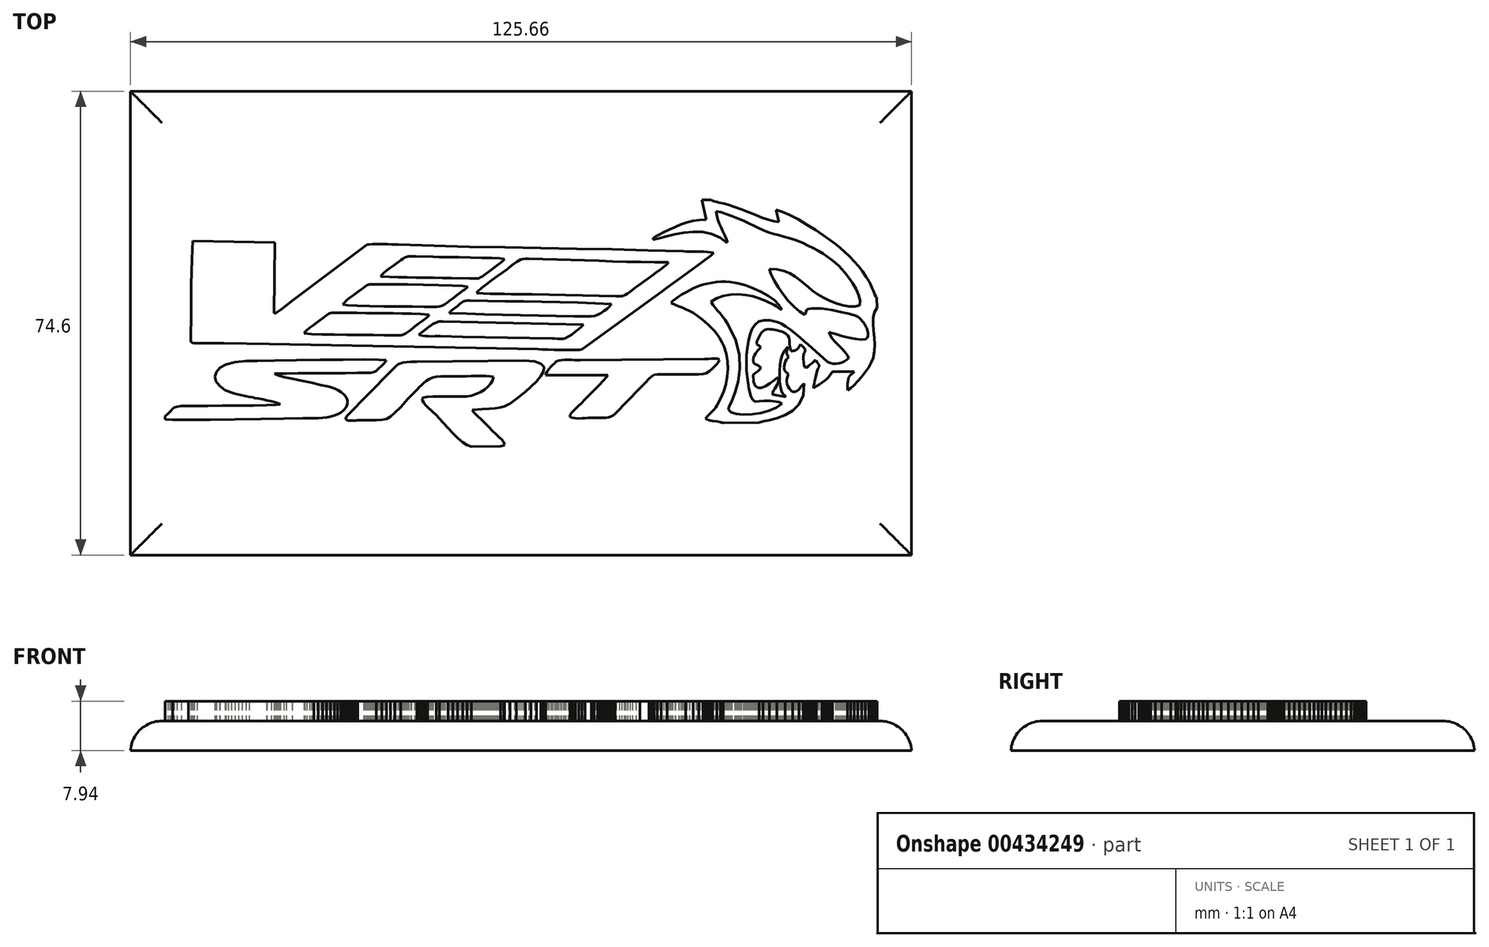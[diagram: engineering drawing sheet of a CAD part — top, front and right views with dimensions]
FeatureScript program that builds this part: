
annotation { "Feature Type Name" : "Feature", "Feature Type Description" : "" }
export const myFeature = defineFeature(function(context is Context, id is Id, definition is map)
    precondition{}
    {
        {
            var Q0;
            Q0=qCreatedBy(makeId("Top.planeOp"),FACE);
            var sketch = newSketch(context, id + "F0", { "sketchPlane" : qUnion([Q0])});
            skLineSegment(sketch, "E0.bottom", {"start": v(62.83, 37.3) * mm, "end": v(-62.83, 37.3) * mm});
            skLineSegment(sketch, "E0.top", {"start": v(62.83, -37.3) * mm, "end": v(-62.83, -37.3) * mm});
            skLineSegment(sketch, "E0.left", {"start": v(62.83, 37.3) * mm, "end": v(62.83, -37.3) * mm});
            skLineSegment(sketch, "E0.right", {"start": v(-62.83, 37.3) * mm, "end": v(-62.83, -37.3) * mm});
            skPoint(sketch, "E0.middle", {"position": v(0, 0) * mm});
            skSolve(sketch);
        }
        {
            var Q0;
            Q0=makeQuery(id+"F0.imprint","IMPRINT",FACE,{"disambiguationData":[TD([[makeQuery(id+"F0.imprint","IMPRINT",EDGE,{"derivedFrom":sQuery(id+"F0.wireOp",EDGE,"E0.bottom")}),1.0]])]});
            extrude(context, id + "F1", {"entities" : qUnion([Q0]), "depth" : 4.76 * mm});
        }
        {
            var Q0;
            Q0=makeQuery(id+"F1.opExtrude","CAP_FACE",FACE,{"disambiguationData":[OSD([sQuery(id+"F0.wireOp",EDGE,"E0.bottom"),sQuery(id+"F0.wireOp",EDGE,"E0.top"),sQuery(id+"F0.wireOp",EDGE,"E0.left"),sQuery(id+"F0.wireOp",EDGE,"E0.right")])],"isStart":false});
            var sketch = newSketch(context, id + "F2", { "sketchPlane" : qUnion([Q0])});
            skLineSegment(sketch, "E1", {"start": v(32.52, -16.06) * mm, "end": v(38.3, -16) * mm});
            skLineSegment(sketch, "E2", {"start": v(38.3, -16) * mm, "end": v(38.94, -15.8) * mm});
            skLineSegment(sketch, "E3", {"start": v(38.94, -15.8) * mm, "end": v(39.95, -15.58) * mm});
            skLineSegment(sketch, "E4", {"start": v(39.95, -15.58) * mm, "end": v(41.18, -15.27) * mm});
            skLineSegment(sketch, "E5", {"start": v(41.18, -15.27) * mm, "end": v(42.49, -14.8) * mm});
            skLineSegment(sketch, "E6", {"start": v(42.49, -14.8) * mm, "end": v(43.73, -14.08) * mm});
            skLineSegment(sketch, "E7", {"start": v(43.73, -14.08) * mm, "end": v(44.75, -13.04) * mm});
            skLineSegment(sketch, "E8", {"start": v(44.75, -13.04) * mm, "end": v(45.42, -11.6) * mm});
            skLineSegment(sketch, "E9", {"start": v(45.42, -11.6) * mm, "end": v(45.57, -9.7) * mm});
            skLineSegment(sketch, "E10", {"start": v(45.57, -9.7) * mm, "end": v(45.33, -9.86) * mm});
            skLineSegment(sketch, "E11", {"start": v(45.33, -9.86) * mm, "end": v(45.15, -10.05) * mm});
            skLineSegment(sketch, "E12", {"start": v(45.15, -10.05) * mm, "end": v(45, -10.27) * mm});
            skLineSegment(sketch, "E13", {"start": v(45, -10.27) * mm, "end": v(44.84, -10.5) * mm});
            skLineSegment(sketch, "E14", {"start": v(44.84, -10.5) * mm, "end": v(44.65, -10.7) * mm});
            skLineSegment(sketch, "E15", {"start": v(44.65, -10.7) * mm, "end": v(44.42, -10.88) * mm});
            skLineSegment(sketch, "E16", {"start": v(44.42, -10.88) * mm, "end": v(44.1, -11) * mm});
            skLineSegment(sketch, "E17", {"start": v(44.1, -11) * mm, "end": v(43.67, -11.04) * mm});
            skLineSegment(sketch, "E18", {"start": v(43.67, -11.04) * mm, "end": v(43.36, -10.77) * mm});
            skLineSegment(sketch, "E19", {"start": v(43.36, -10.77) * mm, "end": v(43.12, -10.48) * mm});
            skLineSegment(sketch, "E20", {"start": v(43.12, -10.48) * mm, "end": v(42.94, -10.16) * mm});
            skLineSegment(sketch, "E21", {"start": v(42.94, -10.16) * mm, "end": v(42.83, -9.81) * mm});
            skLineSegment(sketch, "E22", {"start": v(42.83, -9.81) * mm, "end": v(42.77, -9.44) * mm});
            skLineSegment(sketch, "E23", {"start": v(42.77, -9.44) * mm, "end": v(42.79, -9.04) * mm});
            skLineSegment(sketch, "E24", {"start": v(42.79, -9.04) * mm, "end": v(42.86, -8.61) * mm});
            skLineSegment(sketch, "E25", {"start": v(42.86, -8.61) * mm, "end": v(43, -8.16) * mm});
            skLineSegment(sketch, "E26", {"start": v(43, -8.16) * mm, "end": v(42.52, -7.74) * mm});
            skLineSegment(sketch, "E27", {"start": v(42.52, -7.74) * mm, "end": v(42.4, -7.47) * mm});
            skLineSegment(sketch, "E28", {"start": v(42.4, -7.47) * mm, "end": v(42.34, -7.16) * mm});
            skLineSegment(sketch, "E29", {"start": v(42.34, -7.16) * mm, "end": v(42.35, -6.83) * mm});
            skLineSegment(sketch, "E30", {"start": v(42.35, -6.83) * mm, "end": v(42.42, -6.5) * mm});
            skLineSegment(sketch, "E31", {"start": v(42.42, -6.5) * mm, "end": v(42.53, -6.18) * mm});
            skLineSegment(sketch, "E32", {"start": v(42.53, -6.18) * mm, "end": v(42.68, -5.89) * mm});
            skLineSegment(sketch, "E33", {"start": v(42.68, -5.89) * mm, "end": v(42.86, -5.64) * mm});
            skLineSegment(sketch, "E34", {"start": v(42.86, -5.64) * mm, "end": v(43.06, -5.47) * mm});
            skLineSegment(sketch, "E35", {"start": v(43.06, -5.47) * mm, "end": v(42.97, -5.3) * mm});
            skLineSegment(sketch, "E36", {"start": v(42.97, -5.3) * mm, "end": v(42.86, -5.14) * mm});
            skLineSegment(sketch, "E37", {"start": v(42.86, -5.14) * mm, "end": v(42.81, -5.05) * mm});
            skLineSegment(sketch, "E38", {"start": v(42.81, -5.05) * mm, "end": v(42.77, -4.95) * mm});
            skLineSegment(sketch, "E39", {"start": v(42.77, -4.95) * mm, "end": v(42.75, -4.82) * mm});
            skLineSegment(sketch, "E40", {"start": v(42.75, -4.82) * mm, "end": v(42.74, -4.67) * mm});
            skLineSegment(sketch, "E41", {"start": v(42.74, -4.67) * mm, "end": v(42.77, -4.5) * mm});
            skLineSegment(sketch, "E42", {"start": v(42.77, -4.5) * mm, "end": v(42.83, -4.3) * mm});
            skLineSegment(sketch, "E43", {"start": v(42.83, -4.3) * mm, "end": v(42.9, -4.08) * mm});
            skLineSegment(sketch, "E44", {"start": v(42.9, -4.08) * mm, "end": v(42.92, -3.8) * mm});
            skLineSegment(sketch, "E45", {"start": v(42.92, -3.8) * mm, "end": v(42.45, -4.38) * mm});
            skLineSegment(sketch, "E46", {"start": v(42.45, -4.38) * mm, "end": v(42.09, -5.08) * mm});
            skLineSegment(sketch, "E47", {"start": v(42.09, -5.08) * mm, "end": v(41.84, -5.87) * mm});
            skLineSegment(sketch, "E48", {"start": v(41.84, -5.87) * mm, "end": v(41.68, -6.72) * mm});
            skLineSegment(sketch, "E49", {"start": v(41.68, -6.72) * mm, "end": v(41.6, -7.6) * mm});
            skLineSegment(sketch, "E50", {"start": v(41.6, -7.6) * mm, "end": v(41.6, -8.5) * mm});
            skLineSegment(sketch, "E51", {"start": v(41.6, -8.5) * mm, "end": v(41.64, -9.35) * mm});
            skLineSegment(sketch, "E52", {"start": v(41.64, -9.35) * mm, "end": v(41.73, -10.15) * mm});
            skLineSegment(sketch, "E53", {"start": v(41.73, -10.15) * mm, "end": v(41.78, -10.49) * mm});
            skLineSegment(sketch, "E54", {"start": v(41.78, -10.49) * mm, "end": v(41.85, -10.75) * mm});
            skLineSegment(sketch, "E55", {"start": v(41.85, -10.75) * mm, "end": v(41.92, -10.97) * mm});
            skLineSegment(sketch, "E56", {"start": v(41.92, -10.97) * mm, "end": v(42.02, -11.15) * mm});
            skLineSegment(sketch, "E57", {"start": v(42.02, -11.15) * mm, "end": v(42.14, -11.3) * mm});
            skLineSegment(sketch, "E58", {"start": v(42.14, -11.3) * mm, "end": v(42.28, -11.46) * mm});
            skLineSegment(sketch, "E59", {"start": v(42.28, -11.46) * mm, "end": v(42.44, -11.63) * mm});
            skLineSegment(sketch, "E60", {"start": v(42.44, -11.63) * mm, "end": v(42.64, -11.82) * mm});
            skLineSegment(sketch, "E61", {"start": v(42.64, -11.82) * mm, "end": v(40.45, -11.46) * mm});
            skLineSegment(sketch, "E62", {"start": v(40.45, -11.46) * mm, "end": v(40.54, -11.1) * mm});
            skLineSegment(sketch, "E63", {"start": v(40.54, -11.1) * mm, "end": v(40.7, -10.78) * mm});
            skLineSegment(sketch, "E64", {"start": v(40.7, -10.78) * mm, "end": v(40.88, -10.5) * mm});
            skLineSegment(sketch, "E65", {"start": v(40.88, -10.5) * mm, "end": v(41.07, -10.2) * mm});
            skLineSegment(sketch, "E66", {"start": v(41.07, -10.2) * mm, "end": v(41.24, -9.9) * mm});
            skLineSegment(sketch, "E67", {"start": v(41.24, -9.9) * mm, "end": v(41.36, -9.55) * mm});
            skLineSegment(sketch, "E68", {"start": v(41.36, -9.55) * mm, "end": v(41.41, -9.14) * mm});
            skLineSegment(sketch, "E69", {"start": v(41.41, -9.14) * mm, "end": v(41.36, -8.65) * mm});
            skLineSegment(sketch, "E70", {"start": v(41.36, -8.65) * mm, "end": v(40.7, -9.2) * mm});
            skLineSegment(sketch, "E71", {"start": v(40.7, -9.2) * mm, "end": v(40, -9.71) * mm});
            skLineSegment(sketch, "E72", {"start": v(40, -9.71) * mm, "end": v(39.31, -10.13) * mm});
            skLineSegment(sketch, "E73", {"start": v(39.31, -10.13) * mm, "end": v(38.67, -10.37) * mm});
            skLineSegment(sketch, "E74", {"start": v(38.67, -10.37) * mm, "end": v(38.12, -10.38) * mm});
            skLineSegment(sketch, "E75", {"start": v(38.12, -10.38) * mm, "end": v(37.68, -10.08) * mm});
            skLineSegment(sketch, "E76", {"start": v(37.68, -10.08) * mm, "end": v(37.41, -9.41) * mm});
            skLineSegment(sketch, "E77", {"start": v(37.41, -9.41) * mm, "end": v(37.34, -8.3) * mm});
            skLineSegment(sketch, "E78", {"start": v(37.34, -8.3) * mm, "end": v(37.77, -8) * mm});
            skLineSegment(sketch, "E79", {"start": v(37.77, -8) * mm, "end": v(38.13, -7.73) * mm});
            skLineSegment(sketch, "E80", {"start": v(38.13, -7.73) * mm, "end": v(38.27, -7.6) * mm});
            skLineSegment(sketch, "E81", {"start": v(38.27, -7.6) * mm, "end": v(38.4, -7.47) * mm});
            skLineSegment(sketch, "E82", {"start": v(38.4, -7.47) * mm, "end": v(38.52, -7.31) * mm});
            skLineSegment(sketch, "E83", {"start": v(38.52, -7.31) * mm, "end": v(38.61, -7.13) * mm});
            skLineSegment(sketch, "E84", {"start": v(38.61, -7.13) * mm, "end": v(38.46, -7) * mm});
            skLineSegment(sketch, "E85", {"start": v(38.46, -7) * mm, "end": v(38.3, -6.9) * mm});
            skLineSegment(sketch, "E86", {"start": v(38.3, -6.9) * mm, "end": v(38.16, -6.82) * mm});
            skLineSegment(sketch, "E87", {"start": v(38.16, -6.82) * mm, "end": v(38, -6.74) * mm});
            skLineSegment(sketch, "E88", {"start": v(38, -6.74) * mm, "end": v(37.7, -6.57) * mm});
            skLineSegment(sketch, "E89", {"start": v(37.7, -6.57) * mm, "end": v(37.4, -6.36) * mm});
            skLineSegment(sketch, "E90", {"start": v(37.4, -6.36) * mm, "end": v(37.37, -5.9) * mm});
            skLineSegment(sketch, "E91", {"start": v(37.37, -5.9) * mm, "end": v(37.43, -5.51) * mm});
            skLineSegment(sketch, "E92", {"start": v(37.43, -5.51) * mm, "end": v(37.55, -5.17) * mm});
            skLineSegment(sketch, "E93", {"start": v(37.55, -5.17) * mm, "end": v(37.72, -4.86) * mm});
            skLineSegment(sketch, "E94", {"start": v(37.72, -4.86) * mm, "end": v(37.92, -4.6) * mm});
            skLineSegment(sketch, "E95", {"start": v(37.92, -4.6) * mm, "end": v(38.14, -4.36) * mm});
            skLineSegment(sketch, "E96", {"start": v(38.14, -4.36) * mm, "end": v(38.37, -4.13) * mm});
            skLineSegment(sketch, "E97", {"start": v(38.37, -4.13) * mm, "end": v(38.57, -3.92) * mm});
            skLineSegment(sketch, "E98", {"start": v(38.57, -3.92) * mm, "end": v(38.5, -3.8) * mm});
            skLineSegment(sketch, "E99", {"start": v(38.5, -3.8) * mm, "end": v(38.42, -3.71) * mm});
            skLineSegment(sketch, "E100", {"start": v(38.42, -3.71) * mm, "end": v(38.36, -3.65) * mm});
            skLineSegment(sketch, "E101", {"start": v(38.36, -3.65) * mm, "end": v(38.3, -3.6) * mm});
            skLineSegment(sketch, "E102", {"start": v(38.3, -3.6) * mm, "end": v(38.15, -3.5) * mm});
            skLineSegment(sketch, "E103", {"start": v(38.15, -3.5) * mm, "end": v(37.91, -3.32) * mm});
            skLineSegment(sketch, "E104", {"start": v(37.91, -3.32) * mm, "end": v(37.95, -3.08) * mm});
            skLineSegment(sketch, "E105", {"start": v(37.95, -3.08) * mm, "end": v(38.02, -2.82) * mm});
            skLineSegment(sketch, "E106", {"start": v(38.02, -2.82) * mm, "end": v(38.11, -2.56) * mm});
            skLineSegment(sketch, "E107", {"start": v(38.11, -2.56) * mm, "end": v(38.23, -2.3) * mm});
            skLineSegment(sketch, "E108", {"start": v(38.23, -2.3) * mm, "end": v(38.36, -2.05) * mm});
            skLineSegment(sketch, "E109", {"start": v(38.36, -2.05) * mm, "end": v(38.5, -1.82) * mm});
            skLineSegment(sketch, "E110", {"start": v(38.5, -1.82) * mm, "end": v(38.64, -1.6) * mm});
            skLineSegment(sketch, "E111", {"start": v(38.64, -1.6) * mm, "end": v(38.78, -1.43) * mm});
            skLineSegment(sketch, "E112", {"start": v(38.78, -1.43) * mm, "end": v(39, -1.22) * mm});
            skLineSegment(sketch, "E113", {"start": v(39, -1.22) * mm, "end": v(39.24, -1.08) * mm});
            skLineSegment(sketch, "E114", {"start": v(39.24, -1.08) * mm, "end": v(39.5, -1) * mm});
            skLineSegment(sketch, "E115", {"start": v(39.5, -1) * mm, "end": v(39.8, -0.96) * mm});
            skLineSegment(sketch, "E116", {"start": v(39.8, -0.96) * mm, "end": v(40.11, -0.96) * mm});
            skLineSegment(sketch, "E117", {"start": v(40.11, -0.96) * mm, "end": v(40.44, -1) * mm});
            skLineSegment(sketch, "E118", {"start": v(40.44, -1) * mm, "end": v(40.78, -1.06) * mm});
            skLineSegment(sketch, "E119", {"start": v(40.78, -1.06) * mm, "end": v(41.13, -1.13) * mm});
            skLineSegment(sketch, "E120", {"start": v(41.13, -1.13) * mm, "end": v(42.03, -1.38) * mm});
            skLineSegment(sketch, "E121", {"start": v(42.03, -1.38) * mm, "end": v(42.62, -1.66) * mm});
            skLineSegment(sketch, "E122", {"start": v(42.62, -1.66) * mm, "end": v(42.96, -1.98) * mm});
            skLineSegment(sketch, "E123", {"start": v(42.96, -1.98) * mm, "end": v(43.12, -2.35) * mm});
            skLineSegment(sketch, "E124", {"start": v(43.12, -2.35) * mm, "end": v(43.17, -2.77) * mm});
            skLineSegment(sketch, "E125", {"start": v(43.17, -2.77) * mm, "end": v(43.2, -3.26) * mm});
            skLineSegment(sketch, "E126", {"start": v(43.2, -3.26) * mm, "end": v(43.27, -3.83) * mm});
            skLineSegment(sketch, "E127", {"start": v(43.27, -3.83) * mm, "end": v(43.45, -4.48) * mm});
            skLineSegment(sketch, "E128", {"start": v(43.45, -4.48) * mm, "end": v(43.65, -4.47) * mm});
            skLineSegment(sketch, "E129", {"start": v(43.65, -4.47) * mm, "end": v(43.84, -4.44) * mm});
            skLineSegment(sketch, "E130", {"start": v(43.84, -4.44) * mm, "end": v(44.01, -4.4) * mm});
            skLineSegment(sketch, "E131", {"start": v(44.01, -4.4) * mm, "end": v(44.17, -4.34) * mm});
            skLineSegment(sketch, "E132", {"start": v(44.17, -4.34) * mm, "end": v(44.32, -4.26) * mm});
            skLineSegment(sketch, "E133", {"start": v(44.32, -4.26) * mm, "end": v(44.45, -4.16) * mm});
            skLineSegment(sketch, "E134", {"start": v(44.45, -4.16) * mm, "end": v(44.57, -4.04) * mm});
            skLineSegment(sketch, "E135", {"start": v(44.57, -4.04) * mm, "end": v(44.68, -3.9) * mm});
            skLineSegment(sketch, "E136", {"start": v(44.68, -3.9) * mm, "end": v(44.74, -3.8) * mm});
            skLineSegment(sketch, "E137", {"start": v(44.74, -3.8) * mm, "end": v(44.97, -3.39) * mm});
            skLineSegment(sketch, "E138", {"start": v(44.97, -3.39) * mm, "end": v(45.24, -3.66) * mm});
            skLineSegment(sketch, "E139", {"start": v(45.24, -3.66) * mm, "end": v(45.5, -3.9) * mm});
            skLineSegment(sketch, "E140", {"start": v(45.5, -3.9) * mm, "end": v(45.6, -4.04) * mm});
            skLineSegment(sketch, "E141", {"start": v(45.6, -4.04) * mm, "end": v(45.68, -4.19) * mm});
            skLineSegment(sketch, "E142", {"start": v(45.68, -4.19) * mm, "end": v(45.72, -4.35) * mm});
            skLineSegment(sketch, "E143", {"start": v(45.72, -4.35) * mm, "end": v(45.7, -4.55) * mm});
            skLineSegment(sketch, "E144", {"start": v(45.7, -4.55) * mm, "end": v(45.66, -4.7) * mm});
            skLineSegment(sketch, "E145", {"start": v(45.66, -4.7) * mm, "end": v(45.6, -4.77) * mm});
            skLineSegment(sketch, "E146", {"start": v(45.6, -4.77) * mm, "end": v(45.56, -4.83) * mm});
            skLineSegment(sketch, "E147", {"start": v(45.56, -4.83) * mm, "end": v(45.5, -4.9) * mm});
            skLineSegment(sketch, "E148", {"start": v(45.5, -4.9) * mm, "end": v(45.47, -5.05) * mm});
            skLineSegment(sketch, "E149", {"start": v(45.47, -5.05) * mm, "end": v(45.44, -5.3) * mm});
            skLineSegment(sketch, "E150", {"start": v(45.44, -5.3) * mm, "end": v(45.44, -5.71) * mm});
            skLineSegment(sketch, "E151", {"start": v(45.44, -5.71) * mm, "end": v(45.46, -6.32) * mm});
            skLineSegment(sketch, "E152", {"start": v(45.46, -6.32) * mm, "end": v(45.53, -6.85) * mm});
            skLineSegment(sketch, "E153", {"start": v(45.53, -6.85) * mm, "end": v(45.69, -7.1) * mm});
            skLineSegment(sketch, "E154", {"start": v(45.69, -7.1) * mm, "end": v(45.9, -7.12) * mm});
            skLineSegment(sketch, "E155", {"start": v(45.9, -7.12) * mm, "end": v(46.16, -6.98) * mm});
            skLineSegment(sketch, "E156", {"start": v(46.16, -6.98) * mm, "end": v(46.47, -6.73) * mm});
            skLineSegment(sketch, "E157", {"start": v(46.47, -6.73) * mm, "end": v(46.8, -6.44) * mm});
            skLineSegment(sketch, "E158", {"start": v(46.8, -6.44) * mm, "end": v(47.13, -6.16) * mm});
            skLineSegment(sketch, "E159", {"start": v(47.13, -6.16) * mm, "end": v(47.47, -5.97) * mm});
            skLineSegment(sketch, "E160", {"start": v(47.47, -5.97) * mm, "end": v(47.73, -6.38) * mm});
            skLineSegment(sketch, "E161", {"start": v(47.73, -6.38) * mm, "end": v(47.9, -6.64) * mm});
            skLineSegment(sketch, "E162", {"start": v(47.9, -6.64) * mm, "end": v(47.97, -6.8) * mm});
            skLineSegment(sketch, "E163", {"start": v(47.97, -6.8) * mm, "end": v(47.98, -6.9) * mm});
            skLineSegment(sketch, "E164", {"start": v(47.98, -6.9) * mm, "end": v(47.94, -7.02) * mm});
            skLineSegment(sketch, "E165", {"start": v(47.94, -7.02) * mm, "end": v(47.85, -7.2) * mm});
            skLineSegment(sketch, "E166", {"start": v(47.85, -7.2) * mm, "end": v(47.74, -7.49) * mm});
            skLineSegment(sketch, "E167", {"start": v(47.74, -7.49) * mm, "end": v(47.6, -7.94) * mm});
            skLineSegment(sketch, "E168", {"start": v(47.6, -7.94) * mm, "end": v(47.46, -8.5) * mm});
            skLineSegment(sketch, "E169", {"start": v(47.46, -8.5) * mm, "end": v(47.28, -9.23) * mm});
            skLineSegment(sketch, "E170", {"start": v(47.28, -9.23) * mm, "end": v(47.2, -9.6) * mm});
            skLineSegment(sketch, "E171", {"start": v(47.2, -9.6) * mm, "end": v(47.13, -9.95) * mm});
            skLineSegment(sketch, "E172", {"start": v(47.13, -9.95) * mm, "end": v(47.09, -10.25) * mm});
            skLineSegment(sketch, "E173", {"start": v(47.09, -10.25) * mm, "end": v(47.08, -10.48) * mm});
            skLineSegment(sketch, "E174", {"start": v(47.08, -10.48) * mm, "end": v(47.54, -10.15) * mm});
            skLineSegment(sketch, "E175", {"start": v(47.54, -10.15) * mm, "end": v(47.98, -9.86) * mm});
            skLineSegment(sketch, "E176", {"start": v(47.98, -9.86) * mm, "end": v(48.4, -9.58) * mm});
            skLineSegment(sketch, "E177", {"start": v(48.4, -9.58) * mm, "end": v(48.78, -9.3) * mm});
            skLineSegment(sketch, "E178", {"start": v(48.78, -9.3) * mm, "end": v(49.15, -8.99) * mm});
            skLineSegment(sketch, "E179", {"start": v(49.15, -8.99) * mm, "end": v(49.5, -8.65) * mm});
            skLineSegment(sketch, "E180", {"start": v(49.5, -8.65) * mm, "end": v(49.83, -8.25) * mm});
            skLineSegment(sketch, "E181", {"start": v(49.83, -8.25) * mm, "end": v(50.15, -7.77) * mm});
            skLineSegment(sketch, "E182", {"start": v(50.15, -7.77) * mm, "end": v(53.6, -7.78) * mm});
            skLineSegment(sketch, "E183", {"start": v(53.6, -7.78) * mm, "end": v(53.46, -7.99) * mm});
            skLineSegment(sketch, "E184", {"start": v(53.46, -7.99) * mm, "end": v(53.32, -8.13) * mm});
            skLineSegment(sketch, "E185", {"start": v(53.32, -8.13) * mm, "end": v(53.19, -8.24) * mm});
            skLineSegment(sketch, "E186", {"start": v(53.19, -8.24) * mm, "end": v(53.06, -8.32) * mm});
            skLineSegment(sketch, "E187", {"start": v(53.06, -8.32) * mm, "end": v(52.94, -8.42) * mm});
            skLineSegment(sketch, "E188", {"start": v(52.94, -8.42) * mm, "end": v(52.83, -8.54) * mm});
            skLineSegment(sketch, "E189", {"start": v(52.83, -8.54) * mm, "end": v(52.74, -8.72) * mm});
            skLineSegment(sketch, "E190", {"start": v(52.74, -8.72) * mm, "end": v(52.66, -8.97) * mm});
            skLineSegment(sketch, "E191", {"start": v(52.66, -8.97) * mm, "end": v(52.6, -9.36) * mm});
            skLineSegment(sketch, "E192", {"start": v(52.6, -9.36) * mm, "end": v(52.57, -9.85) * mm});
            skLineSegment(sketch, "E193", {"start": v(52.57, -9.85) * mm, "end": v(52.56, -10.35) * mm});
            skLineSegment(sketch, "E194", {"start": v(52.56, -10.35) * mm, "end": v(52.56, -10.77) * mm});
            skLineSegment(sketch, "E195", {"start": v(52.56, -10.77) * mm, "end": v(53.05, -10.44) * mm});
            skLineSegment(sketch, "E196", {"start": v(53.05, -10.44) * mm, "end": v(53.61, -9.95) * mm});
            skLineSegment(sketch, "E197", {"start": v(53.61, -9.95) * mm, "end": v(54.22, -9.33) * mm});
            skLineSegment(sketch, "E198", {"start": v(54.22, -9.33) * mm, "end": v(54.83, -8.63) * mm});
            skLineSegment(sketch, "E199", {"start": v(54.83, -8.63) * mm, "end": v(55.42, -7.88) * mm});
            skLineSegment(sketch, "E200", {"start": v(55.42, -7.88) * mm, "end": v(55.94, -7.1) * mm});
            skLineSegment(sketch, "E201", {"start": v(55.94, -7.1) * mm, "end": v(56.37, -6.35) * mm});
            skLineSegment(sketch, "E202", {"start": v(56.37, -6.35) * mm, "end": v(56.66, -5.65) * mm});
            skLineSegment(sketch, "E203", {"start": v(56.66, -5.65) * mm, "end": v(56.89, -4.58) * mm});
            skLineSegment(sketch, "E204", {"start": v(56.89, -4.58) * mm, "end": v(56.93, -3.46) * mm});
            skLineSegment(sketch, "E205", {"start": v(56.93, -3.46) * mm, "end": v(56.86, -2.33) * mm});
            skLineSegment(sketch, "E206", {"start": v(56.86, -2.33) * mm, "end": v(56.75, -1.2) * mm});
            skLineSegment(sketch, "E207", {"start": v(56.75, -1.2) * mm, "end": v(56.67, -0.13) * mm});
            skLineSegment(sketch, "E208", {"start": v(56.67, -0.13) * mm, "end": v(56.69, 0.86) * mm});
            skLineSegment(sketch, "E209", {"start": v(56.69, 0.86) * mm, "end": v(56.87, 1.74) * mm});
            skLineSegment(sketch, "E210", {"start": v(56.87, 1.74) * mm, "end": v(57.28, 2.48) * mm});
            skLineSegment(sketch, "E211", {"start": v(57.28, 2.48) * mm, "end": v(57.26, 4) * mm});
            skLineSegment(sketch, "E212", {"start": v(57.26, 4) * mm, "end": v(57.08, 4.3) * mm});
            skLineSegment(sketch, "E213", {"start": v(57.08, 4.3) * mm, "end": v(56.92, 4.62) * mm});
            skLineSegment(sketch, "E214", {"start": v(56.92, 4.62) * mm, "end": v(56.77, 4.95) * mm});
            skLineSegment(sketch, "E215", {"start": v(56.77, 4.95) * mm, "end": v(56.63, 5.3) * mm});
            skLineSegment(sketch, "E216", {"start": v(56.63, 5.3) * mm, "end": v(56.5, 5.65) * mm});
            skLineSegment(sketch, "E217", {"start": v(56.5, 5.65) * mm, "end": v(56.36, 6) * mm});
            skLineSegment(sketch, "E218", {"start": v(56.36, 6) * mm, "end": v(56.2, 6.34) * mm});
            skLineSegment(sketch, "E219", {"start": v(56.2, 6.34) * mm, "end": v(56.04, 6.67) * mm});
            skLineSegment(sketch, "E220", {"start": v(56.04, 6.67) * mm, "end": v(55.55, 7.48) * mm});
            skLineSegment(sketch, "E221", {"start": v(55.55, 7.48) * mm, "end": v(54.97, 8.31) * mm});
            skLineSegment(sketch, "E222", {"start": v(54.97, 8.31) * mm, "end": v(54.32, 9.14) * mm});
            skLineSegment(sketch, "E223", {"start": v(54.32, 9.14) * mm, "end": v(53.61, 9.96) * mm});
            skLineSegment(sketch, "E224", {"start": v(53.61, 9.96) * mm, "end": v(52.87, 10.74) * mm});
            skLineSegment(sketch, "E225", {"start": v(52.87, 10.74) * mm, "end": v(52.12, 11.47) * mm});
            skLineSegment(sketch, "E226", {"start": v(52.12, 11.47) * mm, "end": v(51.36, 12.14) * mm});
            skLineSegment(sketch, "E227", {"start": v(51.36, 12.14) * mm, "end": v(50.63, 12.72) * mm});
            skLineSegment(sketch, "E228", {"start": v(50.63, 12.72) * mm, "end": v(49.77, 13.35) * mm});
            skLineSegment(sketch, "E229", {"start": v(49.77, 13.35) * mm, "end": v(48.66, 14.12) * mm});
            skLineSegment(sketch, "E230", {"start": v(48.66, 14.12) * mm, "end": v(47.37, 14.98) * mm});
            skLineSegment(sketch, "E231", {"start": v(47.37, 14.98) * mm, "end": v(45.98, 15.86) * mm});
            skLineSegment(sketch, "E232", {"start": v(45.98, 15.86) * mm, "end": v(44.57, 16.7) * mm});
            skLineSegment(sketch, "E233", {"start": v(44.57, 16.7) * mm, "end": v(43.23, 17.42) * mm});
            skLineSegment(sketch, "E234", {"start": v(43.23, 17.42) * mm, "end": v(42.02, 17.96) * mm});
            skLineSegment(sketch, "E235", {"start": v(42.02, 17.96) * mm, "end": v(41.03, 18.26) * mm});
            skLineSegment(sketch, "E236", {"start": v(41.03, 18.26) * mm, "end": v(41.49, 16.25) * mm});
            skLineSegment(sketch, "E237", {"start": v(41.49, 16.25) * mm, "end": v(40.69, 16.4) * mm});
            skLineSegment(sketch, "E238", {"start": v(40.69, 16.4) * mm, "end": v(39.78, 16.65) * mm});
            skLineSegment(sketch, "E239", {"start": v(39.78, 16.65) * mm, "end": v(38.78, 17) * mm});
            skLineSegment(sketch, "E240", {"start": v(38.78, 17) * mm, "end": v(37.71, 17.41) * mm});
            skLineSegment(sketch, "E241", {"start": v(37.71, 17.41) * mm, "end": v(36.6, 17.85) * mm});
            skLineSegment(sketch, "E242", {"start": v(36.6, 17.85) * mm, "end": v(35.48, 18.3) * mm});
            skLineSegment(sketch, "E243", {"start": v(35.48, 18.3) * mm, "end": v(34.37, 18.72) * mm});
            skLineSegment(sketch, "E244", {"start": v(34.37, 18.72) * mm, "end": v(33.3, 19.09) * mm});
            skLineSegment(sketch, "E245", {"start": v(33.3, 19.09) * mm, "end": v(32.6, 19.26) * mm});
            skLineSegment(sketch, "E246", {"start": v(32.6, 19.26) * mm, "end": v(31.86, 19.4) * mm});
            skLineSegment(sketch, "E247", {"start": v(31.86, 19.4) * mm, "end": v(31.5, 19.49) * mm});
            skLineSegment(sketch, "E248", {"start": v(31.5, 19.49) * mm, "end": v(31.14, 19.58) * mm});
            skLineSegment(sketch, "E249", {"start": v(31.14, 19.58) * mm, "end": v(30.81, 19.7) * mm});
            skLineSegment(sketch, "E250", {"start": v(30.81, 19.7) * mm, "end": v(30.52, 19.83) * mm});
            skLineSegment(sketch, "E251", {"start": v(30.52, 19.83) * mm, "end": v(29.1, 19.81) * mm});
            skLineSegment(sketch, "E252", {"start": v(29.1, 19.81) * mm, "end": v(29.78, 16.66) * mm});
            skLineSegment(sketch, "E253", {"start": v(29.78, 16.66) * mm, "end": v(28.71, 16.62) * mm});
            skLineSegment(sketch, "E254", {"start": v(28.71, 16.62) * mm, "end": v(27.68, 16.46) * mm});
            skLineSegment(sketch, "E255", {"start": v(27.68, 16.46) * mm, "end": v(26.69, 16.2) * mm});
            skLineSegment(sketch, "E256", {"start": v(26.69, 16.2) * mm, "end": v(25.72, 15.87) * mm});
            skLineSegment(sketch, "E257", {"start": v(25.72, 15.87) * mm, "end": v(24.78, 15.47) * mm});
            skLineSegment(sketch, "E258", {"start": v(24.78, 15.47) * mm, "end": v(23.87, 15.05) * mm});
            skLineSegment(sketch, "E259", {"start": v(23.87, 15.05) * mm, "end": v(22.97, 14.6) * mm});
            skLineSegment(sketch, "E260", {"start": v(22.97, 14.6) * mm, "end": v(22.1, 14.16) * mm});
            skLineSegment(sketch, "E261", {"start": v(22.1, 14.16) * mm, "end": v(21.74, 13.99) * mm});
            skLineSegment(sketch, "E262", {"start": v(21.74, 13.99) * mm, "end": v(21.52, 13.87) * mm});
            skLineSegment(sketch, "E263", {"start": v(21.52, 13.87) * mm, "end": v(21.45, 13.8) * mm});
            skLineSegment(sketch, "E264", {"start": v(21.45, 13.8) * mm, "end": v(21.38, 13.7) * mm});
            skLineSegment(sketch, "E265", {"start": v(21.38, 13.7) * mm, "end": v(21.31, 13.58) * mm});
            skLineSegment(sketch, "E266", {"start": v(21.31, 13.58) * mm, "end": v(21.24, 13.4) * mm});
            skLineSegment(sketch, "E267", {"start": v(21.24, 13.4) * mm, "end": v(22.3, 13.65) * mm});
            skLineSegment(sketch, "E268", {"start": v(22.3, 13.65) * mm, "end": v(23.5, 13.96) * mm});
            skLineSegment(sketch, "E269", {"start": v(23.5, 13.96) * mm, "end": v(24.81, 14.3) * mm});
            skLineSegment(sketch, "E270", {"start": v(24.81, 14.3) * mm, "end": v(26.22, 14.56) * mm});
            skLineSegment(sketch, "E271", {"start": v(26.22, 14.56) * mm, "end": v(27.68, 14.7) * mm});
            skLineSegment(sketch, "E272", {"start": v(27.68, 14.7) * mm, "end": v(29.17, 14.66) * mm});
            skLineSegment(sketch, "E273", {"start": v(29.17, 14.66) * mm, "end": v(30.65, 14.35) * mm});
            skLineSegment(sketch, "E274", {"start": v(30.65, 14.35) * mm, "end": v(32.09, 13.72) * mm});
            skLineSegment(sketch, "E275", {"start": v(32.09, 13.72) * mm, "end": v(32.42, 13.5) * mm});
            skLineSegment(sketch, "E276", {"start": v(32.42, 13.5) * mm, "end": v(32.67, 13.3) * mm});
            skLineSegment(sketch, "E277", {"start": v(32.67, 13.3) * mm, "end": v(32.8, 13.21) * mm});
            skLineSegment(sketch, "E278", {"start": v(32.8, 13.21) * mm, "end": v(32.92, 13.13) * mm});
            skLineSegment(sketch, "E279", {"start": v(32.92, 13.13) * mm, "end": v(33.06, 13.04) * mm});
            skLineSegment(sketch, "E280", {"start": v(33.06, 13.04) * mm, "end": v(33.22, 12.97) * mm});
            skLineSegment(sketch, "E281", {"start": v(33.22, 12.97) * mm, "end": v(33.03, 13.54) * mm});
            skLineSegment(sketch, "E282", {"start": v(33.03, 13.54) * mm, "end": v(32.79, 14.14) * mm});
            skLineSegment(sketch, "E283", {"start": v(32.79, 14.14) * mm, "end": v(32.5, 14.76) * mm});
            skLineSegment(sketch, "E284", {"start": v(32.5, 14.76) * mm, "end": v(32.2, 15.4) * mm});
            skLineSegment(sketch, "E285", {"start": v(32.2, 15.4) * mm, "end": v(31.91, 16.05) * mm});
            skLineSegment(sketch, "E286", {"start": v(31.91, 16.05) * mm, "end": v(31.67, 16.7) * mm});
            skLineSegment(sketch, "E287", {"start": v(31.67, 16.7) * mm, "end": v(31.5, 17.36) * mm});
            skLineSegment(sketch, "E288", {"start": v(31.5, 17.36) * mm, "end": v(31.42, 18) * mm});
            skLineSegment(sketch, "E289", {"start": v(31.42, 18) * mm, "end": v(32.17, 17.84) * mm});
            skLineSegment(sketch, "E290", {"start": v(32.17, 17.84) * mm, "end": v(33.03, 17.58) * mm});
            skLineSegment(sketch, "E291", {"start": v(33.03, 17.58) * mm, "end": v(33.96, 17.24) * mm});
            skLineSegment(sketch, "E292", {"start": v(33.96, 17.24) * mm, "end": v(34.9, 16.85) * mm});
            skLineSegment(sketch, "E293", {"start": v(34.9, 16.85) * mm, "end": v(35.85, 16.44) * mm});
            skLineSegment(sketch, "E294", {"start": v(35.85, 16.44) * mm, "end": v(36.73, 16.03) * mm});
            skLineSegment(sketch, "E295", {"start": v(36.73, 16.03) * mm, "end": v(37.52, 15.65) * mm});
            skLineSegment(sketch, "E296", {"start": v(37.52, 15.65) * mm, "end": v(38.18, 15.3) * mm});
            skLineSegment(sketch, "E297", {"start": v(38.18, 15.3) * mm, "end": v(39, 14.92) * mm});
            skLineSegment(sketch, "E298", {"start": v(39, 14.92) * mm, "end": v(39.8, 14.62) * mm});
            skLineSegment(sketch, "E299", {"start": v(39.8, 14.62) * mm, "end": v(40.59, 14.39) * mm});
            skLineSegment(sketch, "E300", {"start": v(40.59, 14.39) * mm, "end": v(41.4, 14.18) * mm});
            skLineSegment(sketch, "E301", {"start": v(41.4, 14.18) * mm, "end": v(42.25, 13.96) * mm});
            skLineSegment(sketch, "E302", {"start": v(42.25, 13.96) * mm, "end": v(43.17, 13.7) * mm});
            skLineSegment(sketch, "E303", {"start": v(43.17, 13.7) * mm, "end": v(44.2, 13.34) * mm});
            skLineSegment(sketch, "E304", {"start": v(44.2, 13.34) * mm, "end": v(45.36, 12.88) * mm});
            skLineSegment(sketch, "E305", {"start": v(45.36, 12.88) * mm, "end": v(46.2, 12.5) * mm});
            skLineSegment(sketch, "E306", {"start": v(46.2, 12.5) * mm, "end": v(47.02, 12.09) * mm});
            skLineSegment(sketch, "E307", {"start": v(47.02, 12.09) * mm, "end": v(47.81, 11.65) * mm});
            skLineSegment(sketch, "E308", {"start": v(47.81, 11.65) * mm, "end": v(48.57, 11.19) * mm});
            skLineSegment(sketch, "E309", {"start": v(48.57, 11.19) * mm, "end": v(49.3, 10.7) * mm});
            skLineSegment(sketch, "E310", {"start": v(49.3, 10.7) * mm, "end": v(49.98, 10.2) * mm});
            skLineSegment(sketch, "E311", {"start": v(49.98, 10.2) * mm, "end": v(50.62, 9.68) * mm});
            skLineSegment(sketch, "E312", {"start": v(50.62, 9.68) * mm, "end": v(51.2, 9.14) * mm});
            skLineSegment(sketch, "E313", {"start": v(51.2, 9.14) * mm, "end": v(51.6, 8.73) * mm});
            skLineSegment(sketch, "E314", {"start": v(51.6, 8.73) * mm, "end": v(52.13, 8.11) * mm});
            skLineSegment(sketch, "E315", {"start": v(52.13, 8.11) * mm, "end": v(52.75, 7.33) * mm});
            skLineSegment(sketch, "E316", {"start": v(52.75, 7.33) * mm, "end": v(53.37, 6.45) * mm});
            skLineSegment(sketch, "E317", {"start": v(53.37, 6.45) * mm, "end": v(53.93, 5.5) * mm});
            skLineSegment(sketch, "E318", {"start": v(53.93, 5.5) * mm, "end": v(54.34, 4.56) * mm});
            skLineSegment(sketch, "E319", {"start": v(54.34, 4.56) * mm, "end": v(54.55, 3.66) * mm});
            skLineSegment(sketch, "E320", {"start": v(54.55, 3.66) * mm, "end": v(54.48, 2.85) * mm});
            skLineSegment(sketch, "E321", {"start": v(54.48, 2.85) * mm, "end": v(53.72, 2.67) * mm});
            skLineSegment(sketch, "E322", {"start": v(53.72, 2.67) * mm, "end": v(52.8, 2.69) * mm});
            skLineSegment(sketch, "E323", {"start": v(52.8, 2.69) * mm, "end": v(51.78, 2.87) * mm});
            skLineSegment(sketch, "E324", {"start": v(51.78, 2.87) * mm, "end": v(50.7, 3.2) * mm});
            skLineSegment(sketch, "E325", {"start": v(50.7, 3.2) * mm, "end": v(49.63, 3.62) * mm});
            skLineSegment(sketch, "E326", {"start": v(49.63, 3.62) * mm, "end": v(48.6, 4.12) * mm});
            skLineSegment(sketch, "E327", {"start": v(48.6, 4.12) * mm, "end": v(47.68, 4.66) * mm});
            skLineSegment(sketch, "E328", {"start": v(47.68, 4.66) * mm, "end": v(46.9, 5.22) * mm});
            skLineSegment(sketch, "E329", {"start": v(46.9, 5.22) * mm, "end": v(46.23, 5.78) * mm});
            skLineSegment(sketch, "E330", {"start": v(46.23, 5.78) * mm, "end": v(45.56, 6.37) * mm});
            skLineSegment(sketch, "E331", {"start": v(45.56, 6.37) * mm, "end": v(44.85, 6.96) * mm});
            skLineSegment(sketch, "E332", {"start": v(44.85, 6.96) * mm, "end": v(44.1, 7.5) * mm});
            skLineSegment(sketch, "E333", {"start": v(44.1, 7.5) * mm, "end": v(43.25, 8) * mm});
            skLineSegment(sketch, "E334", {"start": v(43.25, 8) * mm, "end": v(42.3, 8.38) * mm});
            skLineSegment(sketch, "E335", {"start": v(42.3, 8.38) * mm, "end": v(41.2, 8.64) * mm});
            skLineSegment(sketch, "E336", {"start": v(41.2, 8.64) * mm, "end": v(39.95, 8.75) * mm});
            skLineSegment(sketch, "E337", {"start": v(39.95, 8.75) * mm, "end": v(40.24, 7.87) * mm});
            skLineSegment(sketch, "E338", {"start": v(40.24, 7.87) * mm, "end": v(40.74, 6.86) * mm});
            skLineSegment(sketch, "E339", {"start": v(40.74, 6.86) * mm, "end": v(41.4, 5.76) * mm});
            skLineSegment(sketch, "E340", {"start": v(41.4, 5.76) * mm, "end": v(42.18, 4.66) * mm});
            skLineSegment(sketch, "E341", {"start": v(42.18, 4.66) * mm, "end": v(43.04, 3.6) * mm});
            skLineSegment(sketch, "E342", {"start": v(43.04, 3.6) * mm, "end": v(43.94, 2.65) * mm});
            skLineSegment(sketch, "E343", {"start": v(43.94, 2.65) * mm, "end": v(44.83, 1.89) * mm});
            skLineSegment(sketch, "E344", {"start": v(44.83, 1.89) * mm, "end": v(45.68, 1.37) * mm});
            skLineSegment(sketch, "E345", {"start": v(45.68, 1.37) * mm, "end": v(45.72, 1.47) * mm});
            skLineSegment(sketch, "E346", {"start": v(45.72, 1.47) * mm, "end": v(45.98, 2.25) * mm});
            skLineSegment(sketch, "E347", {"start": v(45.98, 2.25) * mm, "end": v(46.73, 2.36) * mm});
            skLineSegment(sketch, "E348", {"start": v(46.73, 2.36) * mm, "end": v(47.54, 2.4) * mm});
            skLineSegment(sketch, "E349", {"start": v(47.54, 2.4) * mm, "end": v(48.37, 2.35) * mm});
            skLineSegment(sketch, "E350", {"start": v(48.37, 2.35) * mm, "end": v(49.23, 2.24) * mm});
            skLineSegment(sketch, "E351", {"start": v(49.23, 2.24) * mm, "end": v(50.07, 2.1) * mm});
            skLineSegment(sketch, "E352", {"start": v(50.07, 2.1) * mm, "end": v(50.9, 1.93) * mm});
            skLineSegment(sketch, "E353", {"start": v(50.9, 1.93) * mm, "end": v(51.7, 1.75) * mm});
            skLineSegment(sketch, "E354", {"start": v(51.7, 1.75) * mm, "end": v(52.43, 1.59) * mm});
            skLineSegment(sketch, "E355", {"start": v(52.43, 1.59) * mm, "end": v(52.9, 1.48) * mm});
            skLineSegment(sketch, "E356", {"start": v(52.9, 1.48) * mm, "end": v(53.3, 1.38) * mm});
            skLineSegment(sketch, "E357", {"start": v(53.3, 1.38) * mm, "end": v(53.64, 1.27) * mm});
            skLineSegment(sketch, "E358", {"start": v(53.64, 1.27) * mm, "end": v(53.93, 1.15) * mm});
            skLineSegment(sketch, "E359", {"start": v(53.93, 1.15) * mm, "end": v(54.2, 1) * mm});
            skLineSegment(sketch, "E360", {"start": v(54.2, 1) * mm, "end": v(54.44, 0.83) * mm});
            skLineSegment(sketch, "E361", {"start": v(54.44, 0.83) * mm, "end": v(54.69, 0.6) * mm});
            skLineSegment(sketch, "E362", {"start": v(54.69, 0.6) * mm, "end": v(54.95, 0.3) * mm});
            skLineSegment(sketch, "E363", {"start": v(54.95, 0.3) * mm, "end": v(55.11, 0.1) * mm});
            skLineSegment(sketch, "E364", {"start": v(55.11, 0.1) * mm, "end": v(55.26, -0.12) * mm});
            skLineSegment(sketch, "E365", {"start": v(55.26, -0.12) * mm, "end": v(55.4, -0.35) * mm});
            skLineSegment(sketch, "E366", {"start": v(55.4, -0.35) * mm, "end": v(55.52, -0.58) * mm});
            skLineSegment(sketch, "E367", {"start": v(55.52, -0.58) * mm, "end": v(55.62, -0.83) * mm});
            skLineSegment(sketch, "E368", {"start": v(55.62, -0.83) * mm, "end": v(55.71, -1.08) * mm});
            skLineSegment(sketch, "E369", {"start": v(55.71, -1.08) * mm, "end": v(55.78, -1.33) * mm});
            skLineSegment(sketch, "E370", {"start": v(55.78, -1.33) * mm, "end": v(55.83, -1.6) * mm});
            skLineSegment(sketch, "E371", {"start": v(55.83, -1.6) * mm, "end": v(55.87, -1.96) * mm});
            skLineSegment(sketch, "E372", {"start": v(55.87, -1.96) * mm, "end": v(55.8, -2.27) * mm});
            skLineSegment(sketch, "E373", {"start": v(55.8, -2.27) * mm, "end": v(55.46, -2.56) * mm});
            skLineSegment(sketch, "E374", {"start": v(55.46, -2.56) * mm, "end": v(54.76, -2.63) * mm});
            skLineSegment(sketch, "E375", {"start": v(54.76, -2.63) * mm, "end": v(53.82, -2.54) * mm});
            skLineSegment(sketch, "E376", {"start": v(53.82, -2.54) * mm, "end": v(52.75, -2.33) * mm});
            skLineSegment(sketch, "E377", {"start": v(52.75, -2.33) * mm, "end": v(51.67, -2.06) * mm});
            skLineSegment(sketch, "E378", {"start": v(51.67, -2.06) * mm, "end": v(50.7, -1.78) * mm});
            skLineSegment(sketch, "E379", {"start": v(50.7, -1.78) * mm, "end": v(49.96, -1.55) * mm});
            skLineSegment(sketch, "E380", {"start": v(49.96, -1.55) * mm, "end": v(49.57, -1.43) * mm});
            skLineSegment(sketch, "E381", {"start": v(49.57, -1.43) * mm, "end": v(49.72, -1.9) * mm});
            skLineSegment(sketch, "E382", {"start": v(49.72, -1.9) * mm, "end": v(50.07, -2.44) * mm});
            skLineSegment(sketch, "E383", {"start": v(50.07, -2.44) * mm, "end": v(50.55, -3) * mm});
            skLineSegment(sketch, "E384", {"start": v(50.55, -3) * mm, "end": v(51.1, -3.56) * mm});
            skLineSegment(sketch, "E385", {"start": v(51.1, -3.56) * mm, "end": v(51.65, -4.13) * mm});
            skLineSegment(sketch, "E386", {"start": v(51.65, -4.13) * mm, "end": v(52.16, -4.67) * mm});
            skLineSegment(sketch, "E387", {"start": v(52.16, -4.67) * mm, "end": v(52.54, -5.17) * mm});
            skLineSegment(sketch, "E388", {"start": v(52.54, -5.17) * mm, "end": v(52.76, -5.61) * mm});
            skLineSegment(sketch, "E389", {"start": v(52.76, -5.61) * mm, "end": v(52.44, -5.9) * mm});
            skLineSegment(sketch, "E390", {"start": v(52.44, -5.9) * mm, "end": v(52.06, -6.14) * mm});
            skLineSegment(sketch, "E391", {"start": v(52.06, -6.14) * mm, "end": v(51.63, -6.33) * mm});
            skLineSegment(sketch, "E392", {"start": v(51.63, -6.33) * mm, "end": v(51.17, -6.46) * mm});
            skLineSegment(sketch, "E393", {"start": v(51.17, -6.46) * mm, "end": v(50.7, -6.52) * mm});
            skLineSegment(sketch, "E394", {"start": v(50.7, -6.52) * mm, "end": v(50.22, -6.5) * mm});
            skLineSegment(sketch, "E395", {"start": v(50.22, -6.5) * mm, "end": v(49.75, -6.4) * mm});
            skLineSegment(sketch, "E396", {"start": v(49.75, -6.4) * mm, "end": v(49.32, -6.21) * mm});
            skLineSegment(sketch, "E397", {"start": v(49.32, -6.21) * mm, "end": v(46.8, -4) * mm});
            skLineSegment(sketch, "E398", {"start": v(46.8, -4) * mm, "end": v(46.22, -3.48) * mm});
            skLineSegment(sketch, "E399", {"start": v(46.22, -3.48) * mm, "end": v(45.56, -2.9) * mm});
            skLineSegment(sketch, "E400", {"start": v(45.56, -2.9) * mm, "end": v(44.86, -2.28) * mm});
            skLineSegment(sketch, "E401", {"start": v(44.86, -2.28) * mm, "end": v(44.12, -1.66) * mm});
            skLineSegment(sketch, "E402", {"start": v(44.12, -1.66) * mm, "end": v(43.37, -1.07) * mm});
            skLineSegment(sketch, "E403", {"start": v(43.37, -1.07) * mm, "end": v(42.65, -0.55) * mm});
            skLineSegment(sketch, "E404", {"start": v(42.65, -0.55) * mm, "end": v(41.96, -0.13) * mm});
            skLineSegment(sketch, "E405", {"start": v(41.96, -0.13) * mm, "end": v(41.33, 0.14) * mm});
            skLineSegment(sketch, "E406", {"start": v(41.33, 0.14) * mm, "end": v(40.09, 0.46) * mm});
            skLineSegment(sketch, "E407", {"start": v(40.09, 0.46) * mm, "end": v(39.08, 0.49) * mm});
            skLineSegment(sketch, "E408", {"start": v(39.08, 0.49) * mm, "end": v(38.28, 0.26) * mm});
            skLineSegment(sketch, "E409", {"start": v(38.28, 0.26) * mm, "end": v(37.66, -0.22) * mm});
            skLineSegment(sketch, "E410", {"start": v(37.66, -0.22) * mm, "end": v(37.2, -0.91) * mm});
            skLineSegment(sketch, "E411", {"start": v(37.2, -0.91) * mm, "end": v(36.84, -1.8) * mm});
            skLineSegment(sketch, "E412", {"start": v(36.84, -1.8) * mm, "end": v(36.59, -2.87) * mm});
            skLineSegment(sketch, "E413", {"start": v(36.59, -2.87) * mm, "end": v(36.4, -4.1) * mm});
            skLineSegment(sketch, "E414", {"start": v(36.4, -4.1) * mm, "end": v(36.34, -4.62) * mm});
            skLineSegment(sketch, "E415", {"start": v(36.34, -4.62) * mm, "end": v(36.3, -5.18) * mm});
            skLineSegment(sketch, "E416", {"start": v(36.3, -5.18) * mm, "end": v(36.27, -5.76) * mm});
            skLineSegment(sketch, "E417", {"start": v(36.27, -5.76) * mm, "end": v(36.27, -6.36) * mm});
            skLineSegment(sketch, "E418", {"start": v(36.27, -6.36) * mm, "end": v(36.28, -6.95) * mm});
            skLineSegment(sketch, "E419", {"start": v(36.28, -6.95) * mm, "end": v(36.3, -7.53) * mm});
            skLineSegment(sketch, "E420", {"start": v(36.3, -7.53) * mm, "end": v(36.34, -8.1) * mm});
            skLineSegment(sketch, "E421", {"start": v(36.34, -8.1) * mm, "end": v(36.4, -8.64) * mm});
            skLineSegment(sketch, "E422", {"start": v(36.4, -8.64) * mm, "end": v(36.68, -10.55) * mm});
            skLineSegment(sketch, "E423", {"start": v(36.68, -10.55) * mm, "end": v(36.96, -11.74) * mm});
            skLineSegment(sketch, "E424", {"start": v(36.96, -11.74) * mm, "end": v(37.3, -12.37) * mm});
            skLineSegment(sketch, "E425", {"start": v(37.3, -12.37) * mm, "end": v(37.73, -12.6) * mm});
            skLineSegment(sketch, "E426", {"start": v(37.73, -12.6) * mm, "end": v(38.32, -12.58) * mm});
            skLineSegment(sketch, "E427", {"start": v(38.32, -12.58) * mm, "end": v(39.11, -12.48) * mm});
            skLineSegment(sketch, "E428", {"start": v(39.11, -12.48) * mm, "end": v(40.15, -12.46) * mm});
            skLineSegment(sketch, "E429", {"start": v(40.15, -12.46) * mm, "end": v(41.48, -12.67) * mm});
            skLineSegment(sketch, "E430", {"start": v(41.48, -12.67) * mm, "end": v(42, -12.9) * mm});
            skLineSegment(sketch, "E431", {"start": v(42, -12.9) * mm, "end": v(41.12, -13.57) * mm});
            skLineSegment(sketch, "E432", {"start": v(41.12, -13.57) * mm, "end": v(39.93, -14.08) * mm});
            skLineSegment(sketch, "E433", {"start": v(39.93, -14.08) * mm, "end": v(38.57, -14.44) * mm});
            skLineSegment(sketch, "E434", {"start": v(38.57, -14.44) * mm, "end": v(37.15, -14.63) * mm});
            skLineSegment(sketch, "E435", {"start": v(37.15, -14.63) * mm, "end": v(35.8, -14.68) * mm});
            skLineSegment(sketch, "E436", {"start": v(35.8, -14.68) * mm, "end": v(34.64, -14.57) * mm});
            skLineSegment(sketch, "E437", {"start": v(34.64, -14.57) * mm, "end": v(33.79, -14.31) * mm});
            skLineSegment(sketch, "E438", {"start": v(33.79, -14.31) * mm, "end": v(33.37, -13.9) * mm});
            skLineSegment(sketch, "E439", {"start": v(33.37, -13.9) * mm, "end": v(33.5, -13.45) * mm});
            skLineSegment(sketch, "E440", {"start": v(33.5, -13.45) * mm, "end": v(33.9, -12.5) * mm});
            skLineSegment(sketch, "E441", {"start": v(33.9, -12.5) * mm, "end": v(34.43, -11.14) * mm});
            skLineSegment(sketch, "E442", {"start": v(34.43, -11.14) * mm, "end": v(34.92, -9.4) * mm});
            skLineSegment(sketch, "E443", {"start": v(34.92, -9.4) * mm, "end": v(35.2, -7.37) * mm});
            skLineSegment(sketch, "E444", {"start": v(35.2, -7.37) * mm, "end": v(35.12, -5.07) * mm});
            skLineSegment(sketch, "E445", {"start": v(35.12, -5.07) * mm, "end": v(34.5, -2.6) * mm});
            skLineSegment(sketch, "E446", {"start": v(34.5, -2.6) * mm, "end": v(33.2, 0.03) * mm});
            skLineSegment(sketch, "E447", {"start": v(33.2, 0.03) * mm, "end": v(32.84, 0.54) * mm});
            skLineSegment(sketch, "E448", {"start": v(32.84, 0.54) * mm, "end": v(32.44, 1.07) * mm});
            skLineSegment(sketch, "E449", {"start": v(32.44, 1.07) * mm, "end": v(32.02, 1.6) * mm});
            skLineSegment(sketch, "E450", {"start": v(32.02, 1.6) * mm, "end": v(31.6, 2.09) * mm});
            skLineSegment(sketch, "E451", {"start": v(31.6, 2.09) * mm, "end": v(31.22, 2.54) * mm});
            skLineSegment(sketch, "E452", {"start": v(31.22, 2.54) * mm, "end": v(30.9, 2.93) * mm});
            skLineSegment(sketch, "E453", {"start": v(30.9, 2.93) * mm, "end": v(30.67, 3.25) * mm});
            skLineSegment(sketch, "E454", {"start": v(30.67, 3.25) * mm, "end": v(30.55, 3.48) * mm});
            skLineSegment(sketch, "E455", {"start": v(30.55, 3.48) * mm, "end": v(31.53, 4.02) * mm});
            skLineSegment(sketch, "E456", {"start": v(31.53, 4.02) * mm, "end": v(32.61, 4.38) * mm});
            skLineSegment(sketch, "E457", {"start": v(32.61, 4.38) * mm, "end": v(33.75, 4.58) * mm});
            skLineSegment(sketch, "E458", {"start": v(33.75, 4.58) * mm, "end": v(34.93, 4.63) * mm});
            skLineSegment(sketch, "E459", {"start": v(34.93, 4.63) * mm, "end": v(36.13, 4.54) * mm});
            skLineSegment(sketch, "E460", {"start": v(36.13, 4.54) * mm, "end": v(37.3, 4.32) * mm});
            skLineSegment(sketch, "E461", {"start": v(37.3, 4.32) * mm, "end": v(38.44, 3.98) * mm});
            skLineSegment(sketch, "E462", {"start": v(38.44, 3.98) * mm, "end": v(39.51, 3.54) * mm});
            skLineSegment(sketch, "E463", {"start": v(39.51, 3.54) * mm, "end": v(40.72, 2.92) * mm});
            skLineSegment(sketch, "E464", {"start": v(40.72, 2.92) * mm, "end": v(41.02, 2.73) * mm});
            skLineSegment(sketch, "E465", {"start": v(41.02, 2.73) * mm, "end": v(41.34, 2.52) * mm});
            skLineSegment(sketch, "E466", {"start": v(41.34, 2.52) * mm, "end": v(41.5, 2.42) * mm});
            skLineSegment(sketch, "E467", {"start": v(41.5, 2.42) * mm, "end": v(41.67, 2.32) * mm});
            skLineSegment(sketch, "E468", {"start": v(41.67, 2.32) * mm, "end": v(41.83, 2.24) * mm});
            skLineSegment(sketch, "E469", {"start": v(41.83, 2.24) * mm, "end": v(41.99, 2.17) * mm});
            skLineSegment(sketch, "E470", {"start": v(41.99, 2.17) * mm, "end": v(41.52, 2.93) * mm});
            skLineSegment(sketch, "E471", {"start": v(41.52, 2.93) * mm, "end": v(40.76, 3.68) * mm});
            skLineSegment(sketch, "E472", {"start": v(40.76, 3.68) * mm, "end": v(39.77, 4.4) * mm});
            skLineSegment(sketch, "E473", {"start": v(39.77, 4.4) * mm, "end": v(38.62, 5.06) * mm});
            skLineSegment(sketch, "E474", {"start": v(38.62, 5.06) * mm, "end": v(37.37, 5.64) * mm});
            skLineSegment(sketch, "E475", {"start": v(37.37, 5.64) * mm, "end": v(36.09, 6.12) * mm});
            skLineSegment(sketch, "E476", {"start": v(36.09, 6.12) * mm, "end": v(34.83, 6.46) * mm});
            skLineSegment(sketch, "E477", {"start": v(34.83, 6.46) * mm, "end": v(33.66, 6.65) * mm});
            skLineSegment(sketch, "E478", {"start": v(33.66, 6.65) * mm, "end": v(32.93, 6.7) * mm});
            skLineSegment(sketch, "E479", {"start": v(32.93, 6.7) * mm, "end": v(32.2, 6.68) * mm});
            skLineSegment(sketch, "E480", {"start": v(32.2, 6.68) * mm, "end": v(31.47, 6.63) * mm});
            skLineSegment(sketch, "E481", {"start": v(31.47, 6.63) * mm, "end": v(30.76, 6.53) * mm});
            skLineSegment(sketch, "E482", {"start": v(30.76, 6.53) * mm, "end": v(30.07, 6.4) * mm});
            skLineSegment(sketch, "E483", {"start": v(30.07, 6.4) * mm, "end": v(29.4, 6.22) * mm});
            skLineSegment(sketch, "E484", {"start": v(29.4, 6.22) * mm, "end": v(28.77, 6.03) * mm});
            skLineSegment(sketch, "E485", {"start": v(28.77, 6.03) * mm, "end": v(28.17, 5.8) * mm});
            skLineSegment(sketch, "E486", {"start": v(28.17, 5.8) * mm, "end": v(27.7, 5.6) * mm});
            skLineSegment(sketch, "E487", {"start": v(27.7, 5.6) * mm, "end": v(27.15, 5.32) * mm});
            skLineSegment(sketch, "E488", {"start": v(27.15, 5.32) * mm, "end": v(26.55, 4.99) * mm});
            skLineSegment(sketch, "E489", {"start": v(26.55, 4.99) * mm, "end": v(25.94, 4.63) * mm});
            skLineSegment(sketch, "E490", {"start": v(25.94, 4.63) * mm, "end": v(25.36, 4.25) * mm});
            skLineSegment(sketch, "E491", {"start": v(25.36, 4.25) * mm, "end": v(24.84, 3.89) * mm});
            skLineSegment(sketch, "E492", {"start": v(24.84, 3.89) * mm, "end": v(24.43, 3.55) * mm});
            skLineSegment(sketch, "E493", {"start": v(24.43, 3.55) * mm, "end": v(24.15, 3.26) * mm});
            skLineSegment(sketch, "E494", {"start": v(24.15, 3.26) * mm, "end": v(24.84, 2.94) * mm});
            skLineSegment(sketch, "E495", {"start": v(24.84, 2.94) * mm, "end": v(25.44, 2.7) * mm});
            skLineSegment(sketch, "E496", {"start": v(25.44, 2.7) * mm, "end": v(26, 2.48) * mm});
            skLineSegment(sketch, "E497", {"start": v(26, 2.48) * mm, "end": v(26.53, 2.25) * mm});
            skLineSegment(sketch, "E498", {"start": v(26.53, 2.25) * mm, "end": v(27.1, 1.99) * mm});
            skLineSegment(sketch, "E499", {"start": v(27.1, 1.99) * mm, "end": v(27.7, 1.64) * mm});
            skLineSegment(sketch, "E500", {"start": v(27.7, 1.64) * mm, "end": v(28.39, 1.18) * mm});
            skLineSegment(sketch, "E501", {"start": v(28.39, 1.18) * mm, "end": v(29.2, 0.57) * mm});
            skLineSegment(sketch, "E502", {"start": v(29.2, 0.57) * mm, "end": v(29.67, 0.17) * mm});
            skLineSegment(sketch, "E503", {"start": v(29.67, 0.17) * mm, "end": v(30.15, -0.26) * mm});
            skLineSegment(sketch, "E504", {"start": v(30.15, -0.26) * mm, "end": v(30.64, -0.74) * mm});
            skLineSegment(sketch, "E505", {"start": v(30.64, -0.74) * mm, "end": v(31.11, -1.26) * mm});
            skLineSegment(sketch, "E506", {"start": v(31.11, -1.26) * mm, "end": v(31.56, -1.82) * mm});
            skLineSegment(sketch, "E507", {"start": v(31.56, -1.82) * mm, "end": v(31.98, -2.42) * mm});
            skLineSegment(sketch, "E508", {"start": v(31.98, -2.42) * mm, "end": v(32.36, -3.06) * mm});
            skLineSegment(sketch, "E509", {"start": v(32.36, -3.06) * mm, "end": v(32.68, -3.75) * mm});
            skLineSegment(sketch, "E510", {"start": v(32.68, -3.75) * mm, "end": v(33.06, -4.9) * mm});
            skLineSegment(sketch, "E511", {"start": v(33.06, -4.9) * mm, "end": v(33.26, -6.1) * mm});
            skLineSegment(sketch, "E512", {"start": v(33.26, -6.1) * mm, "end": v(33.3, -7.35) * mm});
            skLineSegment(sketch, "E513", {"start": v(33.3, -7.35) * mm, "end": v(33.2, -8.6) * mm});
            skLineSegment(sketch, "E514", {"start": v(33.2, -8.6) * mm, "end": v(32.96, -9.84) * mm});
            skLineSegment(sketch, "E515", {"start": v(32.96, -9.84) * mm, "end": v(32.6, -11.04) * mm});
            skLineSegment(sketch, "E516", {"start": v(32.6, -11.04) * mm, "end": v(32.12, -12.18) * mm});
            skLineSegment(sketch, "E517", {"start": v(32.12, -12.18) * mm, "end": v(31.54, -13.23) * mm});
            skLineSegment(sketch, "E518", {"start": v(31.54, -13.23) * mm, "end": v(31.33, -13.54) * mm});
            skLineSegment(sketch, "E519", {"start": v(31.33, -13.54) * mm, "end": v(31.1, -13.83) * mm});
            skLineSegment(sketch, "E520", {"start": v(31.1, -13.83) * mm, "end": v(30.88, -14.1) * mm});
            skLineSegment(sketch, "E521", {"start": v(30.88, -14.1) * mm, "end": v(30.64, -14.35) * mm});
            skLineSegment(sketch, "E522", {"start": v(30.64, -14.35) * mm, "end": v(30.15, -14.84) * mm});
            skLineSegment(sketch, "E523", {"start": v(30.15, -14.84) * mm, "end": v(29.67, -15.32) * mm});
            skLineSegment(sketch, "E524", {"start": v(29.67, -15.32) * mm, "end": v(29.93, -15.48) * mm});
            skLineSegment(sketch, "E525", {"start": v(29.93, -15.48) * mm, "end": v(30.22, -15.58) * mm});
            skLineSegment(sketch, "E526", {"start": v(30.22, -15.58) * mm, "end": v(30.53, -15.66) * mm});
            skLineSegment(sketch, "E527", {"start": v(30.53, -15.66) * mm, "end": v(30.84, -15.72) * mm});
            skLineSegment(sketch, "E528", {"start": v(30.84, -15.72) * mm, "end": v(31.49, -15.8) * mm});
            skLineSegment(sketch, "E529", {"start": v(31.49, -15.8) * mm, "end": v(32.11, -15.92) * mm});
            skLineSegment(sketch, "E530", {"start": v(32.11, -15.92) * mm, "end": v(32.25, -15.96) * mm});
            skLineSegment(sketch, "E531", {"start": v(32.25, -15.96) * mm, "end": v(32.38, -16) * mm});
            skLineSegment(sketch, "E532", {"start": v(32.38, -16) * mm, "end": v(32.52, -16.06) * mm});
            skLineSegment(sketch, "E533", {"start": v(-4.42, -8.64) * mm, "end": v(-4.55, -9.19) * mm});
            skLineSegment(sketch, "E534", {"start": v(-4.55, -9.19) * mm, "end": v(-4.85, -9.72) * mm});
            skLineSegment(sketch, "E535", {"start": v(-4.85, -9.72) * mm, "end": v(-5.3, -10.22) * mm});
            skLineSegment(sketch, "E536", {"start": v(-5.3, -10.22) * mm, "end": v(-5.88, -10.68) * mm});
            skLineSegment(sketch, "E537", {"start": v(-5.88, -10.68) * mm, "end": v(-6.54, -11.08) * mm});
            skLineSegment(sketch, "E538", {"start": v(-6.54, -11.08) * mm, "end": v(-7.25, -11.4) * mm});
            skLineSegment(sketch, "E539", {"start": v(-7.25, -11.4) * mm, "end": v(-7.98, -11.64) * mm});
            skLineSegment(sketch, "E540", {"start": v(-7.98, -11.64) * mm, "end": v(-8.7, -11.77) * mm});
            skLineSegment(sketch, "E541", {"start": v(-8.7, -11.77) * mm, "end": v(-9.52, -11.8) * mm});
            skLineSegment(sketch, "E542", {"start": v(-9.52, -11.8) * mm, "end": v(-10.57, -11.8) * mm});
            skLineSegment(sketch, "E543", {"start": v(-10.57, -11.8) * mm, "end": v(-11.76, -11.77) * mm});
            skLineSegment(sketch, "E544", {"start": v(-11.76, -11.77) * mm, "end": v(-12.98, -11.76) * mm});
            skLineSegment(sketch, "E545", {"start": v(-12.98, -11.76) * mm, "end": v(-14.12, -11.77) * mm});
            skLineSegment(sketch, "E546", {"start": v(-14.12, -11.77) * mm, "end": v(-15.06, -11.83) * mm});
            skLineSegment(sketch, "E547", {"start": v(-15.06, -11.83) * mm, "end": v(-15.7, -11.96) * mm});
            skLineSegment(sketch, "E548", {"start": v(-15.7, -11.96) * mm, "end": v(-15.95, -12.19) * mm});
            skLineSegment(sketch, "E549", {"start": v(-15.95, -12.19) * mm, "end": v(-15.87, -12.45) * mm});
            skLineSegment(sketch, "E550", {"start": v(-15.87, -12.45) * mm, "end": v(-15.67, -12.77) * mm});
            skLineSegment(sketch, "E551", {"start": v(-15.67, -12.77) * mm, "end": v(-15.38, -13.11) * mm});
            skLineSegment(sketch, "E552", {"start": v(-15.38, -13.11) * mm, "end": v(-15.03, -13.48) * mm});
            skLineSegment(sketch, "E553", {"start": v(-15.03, -13.48) * mm, "end": v(-14.27, -14.2) * mm});
            skLineSegment(sketch, "E554", {"start": v(-14.27, -14.2) * mm, "end": v(-13.63, -14.8) * mm});
            skLineSegment(sketch, "E555", {"start": v(-13.63, -14.8) * mm, "end": v(-13.12, -15.36) * mm});
            skLineSegment(sketch, "E556", {"start": v(-13.12, -15.36) * mm, "end": v(-12.48, -16.07) * mm});
            skLineSegment(sketch, "E557", {"start": v(-12.48, -16.07) * mm, "end": v(-11.75, -16.88) * mm});
            skLineSegment(sketch, "E558", {"start": v(-11.75, -16.88) * mm, "end": v(-10.97, -17.7) * mm});
            skLineSegment(sketch, "E559", {"start": v(-10.97, -17.7) * mm, "end": v(-10.17, -18.48) * mm});
            skLineSegment(sketch, "E560", {"start": v(-10.17, -18.48) * mm, "end": v(-9.38, -19.13) * mm});
            skLineSegment(sketch, "E561", {"start": v(-9.38, -19.13) * mm, "end": v(-8.65, -19.6) * mm});
            skLineSegment(sketch, "E562", {"start": v(-8.65, -19.6) * mm, "end": v(-8, -19.83) * mm});
            skLineSegment(sketch, "E563", {"start": v(-8, -19.83) * mm, "end": v(-3.28, -19.8) * mm});
            skLineSegment(sketch, "E564", {"start": v(-3.28, -19.8) * mm, "end": v(-2.8, -19.68) * mm});
            skLineSegment(sketch, "E565", {"start": v(-2.8, -19.68) * mm, "end": v(-2.64, -19.46) * mm});
            skLineSegment(sketch, "E566", {"start": v(-2.64, -19.46) * mm, "end": v(-2.75, -19.16) * mm});
            skLineSegment(sketch, "E567", {"start": v(-2.75, -19.16) * mm, "end": v(-3.05, -18.77) * mm});
            skLineSegment(sketch, "E568", {"start": v(-3.05, -18.77) * mm, "end": v(-3.5, -18.33) * mm});
            skLineSegment(sketch, "E569", {"start": v(-3.5, -18.33) * mm, "end": v(-4.04, -17.84) * mm});
            skLineSegment(sketch, "E570", {"start": v(-4.04, -17.84) * mm, "end": v(-4.6, -17.31) * mm});
            skLineSegment(sketch, "E571", {"start": v(-4.6, -17.31) * mm, "end": v(-5.12, -16.76) * mm});
            skLineSegment(sketch, "E572", {"start": v(-5.12, -16.76) * mm, "end": v(-5.45, -16.4) * mm});
            skLineSegment(sketch, "E573", {"start": v(-5.45, -16.4) * mm, "end": v(-5.8, -16.04) * mm});
            skLineSegment(sketch, "E574", {"start": v(-5.8, -16.04) * mm, "end": v(-6.17, -15.7) * mm});
            skLineSegment(sketch, "E575", {"start": v(-6.17, -15.7) * mm, "end": v(-6.54, -15.35) * mm});
            skLineSegment(sketch, "E576", {"start": v(-6.54, -15.35) * mm, "end": v(-6.9, -15) * mm});
            skLineSegment(sketch, "E577", {"start": v(-6.9, -15) * mm, "end": v(-7.25, -14.66) * mm});
            skLineSegment(sketch, "E578", {"start": v(-7.25, -14.66) * mm, "end": v(-7.58, -14.31) * mm});
            skLineSegment(sketch, "E579", {"start": v(-7.58, -14.31) * mm, "end": v(-7.87, -13.96) * mm});
            skLineSegment(sketch, "E580", {"start": v(-7.87, -13.96) * mm, "end": v(-6.28, -13.8) * mm});
            skLineSegment(sketch, "E581", {"start": v(-6.28, -13.8) * mm, "end": v(-5.09, -13.73) * mm});
            skLineSegment(sketch, "E582", {"start": v(-5.09, -13.73) * mm, "end": v(-4.16, -13.69) * mm});
            skLineSegment(sketch, "E583", {"start": v(-4.16, -13.69) * mm, "end": v(-3.38, -13.6) * mm});
            skLineSegment(sketch, "E584", {"start": v(-3.38, -13.6) * mm, "end": v(-2.63, -13.36) * mm});
            skLineSegment(sketch, "E585", {"start": v(-2.63, -13.36) * mm, "end": v(-1.78, -12.9) * mm});
            skLineSegment(sketch, "E586", {"start": v(-1.78, -12.9) * mm, "end": v(-0.71, -12.15) * mm});
            skLineSegment(sketch, "E587", {"start": v(-0.71, -12.15) * mm, "end": v(0.7, -11.02) * mm});
            skLineSegment(sketch, "E588", {"start": v(0.7, -11.02) * mm, "end": v(1.63, -10.2) * mm});
            skLineSegment(sketch, "E589", {"start": v(1.63, -10.2) * mm, "end": v(2.5, -9.35) * mm});
            skLineSegment(sketch, "E590", {"start": v(2.5, -9.35) * mm, "end": v(3.21, -8.5) * mm});
            skLineSegment(sketch, "E591", {"start": v(3.21, -8.5) * mm, "end": v(3.64, -7.72) * mm});
            skLineSegment(sketch, "E592", {"start": v(3.64, -7.72) * mm, "end": v(3.68, -7.03) * mm});
            skLineSegment(sketch, "E593", {"start": v(3.68, -7.03) * mm, "end": v(3.22, -6.49) * mm});
            skLineSegment(sketch, "E594", {"start": v(3.22, -6.49) * mm, "end": v(2.17, -6.14) * mm});
            skLineSegment(sketch, "E595", {"start": v(2.17, -6.14) * mm, "end": v(0.4, -6.03) * mm});
            skLineSegment(sketch, "E596", {"start": v(0.4, -6.03) * mm, "end": v(-16.71, -6.2) * mm});
            skLineSegment(sketch, "E597", {"start": v(-16.71, -6.2) * mm, "end": v(-17.66, -6.22) * mm});
            skLineSegment(sketch, "E598", {"start": v(-17.66, -6.22) * mm, "end": v(-18.38, -6.25) * mm});
            skLineSegment(sketch, "E599", {"start": v(-18.38, -6.25) * mm, "end": v(-18.93, -6.31) * mm});
            skLineSegment(sketch, "E600", {"start": v(-18.93, -6.31) * mm, "end": v(-19.37, -6.43) * mm});
            skLineSegment(sketch, "E601", {"start": v(-19.37, -6.43) * mm, "end": v(-19.74, -6.61) * mm});
            skLineSegment(sketch, "E602", {"start": v(-19.74, -6.61) * mm, "end": v(-20.1, -6.89) * mm});
            skLineSegment(sketch, "E603", {"start": v(-20.1, -6.89) * mm, "end": v(-20.5, -7.27) * mm});
            skLineSegment(sketch, "E604", {"start": v(-20.5, -7.27) * mm, "end": v(-21, -7.77) * mm});
            skLineSegment(sketch, "E605", {"start": v(-21, -7.77) * mm, "end": v(-28.05, -14.96) * mm});
            skLineSegment(sketch, "E606", {"start": v(-28.05, -14.96) * mm, "end": v(-28.2, -15.27) * mm});
            skLineSegment(sketch, "E607", {"start": v(-28.2, -15.27) * mm, "end": v(-28.16, -15.47) * mm});
            skLineSegment(sketch, "E608", {"start": v(-28.16, -15.47) * mm, "end": v(-27.98, -15.6) * mm});
            skLineSegment(sketch, "E609", {"start": v(-27.98, -15.6) * mm, "end": v(-27.7, -15.66) * mm});
            skLineSegment(sketch, "E610", {"start": v(-27.7, -15.66) * mm, "end": v(-27.34, -15.67) * mm});
            skLineSegment(sketch, "E611", {"start": v(-27.34, -15.67) * mm, "end": v(-26.96, -15.66) * mm});
            skLineSegment(sketch, "E612", {"start": v(-26.96, -15.66) * mm, "end": v(-26.58, -15.63) * mm});
            skLineSegment(sketch, "E613", {"start": v(-26.58, -15.63) * mm, "end": v(-26.24, -15.62) * mm});
            skLineSegment(sketch, "E614", {"start": v(-26.24, -15.62) * mm, "end": v(-24.55, -15.61) * mm});
            skLineSegment(sketch, "E615", {"start": v(-24.55, -15.61) * mm, "end": v(-23.3, -15.61) * mm});
            skLineSegment(sketch, "E616", {"start": v(-23.3, -15.61) * mm, "end": v(-22.38, -15.56) * mm});
            skLineSegment(sketch, "E617", {"start": v(-22.38, -15.56) * mm, "end": v(-21.65, -15.38) * mm});
            skLineSegment(sketch, "E618", {"start": v(-21.65, -15.38) * mm, "end": v(-20.99, -15.02) * mm});
            skLineSegment(sketch, "E619", {"start": v(-20.99, -15.02) * mm, "end": v(-20.27, -14.4) * mm});
            skLineSegment(sketch, "E620", {"start": v(-20.27, -14.4) * mm, "end": v(-19.38, -13.49) * mm});
            skLineSegment(sketch, "E621", {"start": v(-19.38, -13.49) * mm, "end": v(-18.17, -12.2) * mm});
            skLineSegment(sketch, "E622", {"start": v(-18.17, -12.2) * mm, "end": v(-17.5, -11.48) * mm});
            skLineSegment(sketch, "E623", {"start": v(-17.5, -11.48) * mm, "end": v(-16.75, -10.69) * mm});
            skLineSegment(sketch, "E624", {"start": v(-16.75, -10.69) * mm, "end": v(-16.37, -10.3) * mm});
            skLineSegment(sketch, "E625", {"start": v(-16.37, -10.3) * mm, "end": v(-15.99, -9.92) * mm});
            skLineSegment(sketch, "E626", {"start": v(-15.99, -9.92) * mm, "end": v(-15.62, -9.58) * mm});
            skLineSegment(sketch, "E627", {"start": v(-15.62, -9.58) * mm, "end": v(-15.28, -9.29) * mm});
            skLineSegment(sketch, "E628", {"start": v(-15.28, -9.29) * mm, "end": v(-14.8, -8.98) * mm});
            skLineSegment(sketch, "E629", {"start": v(-14.8, -8.98) * mm, "end": v(-14.23, -8.77) * mm});
            skLineSegment(sketch, "E630", {"start": v(-14.23, -8.77) * mm, "end": v(-13.6, -8.64) * mm});
            skLineSegment(sketch, "E631", {"start": v(-13.6, -8.64) * mm, "end": v(-12.93, -8.57) * mm});
            skLineSegment(sketch, "E632", {"start": v(-12.93, -8.57) * mm, "end": v(-12.24, -8.55) * mm});
            skLineSegment(sketch, "E633", {"start": v(-12.24, -8.55) * mm, "end": v(-11.52, -8.56) * mm});
            skLineSegment(sketch, "E634", {"start": v(-11.52, -8.56) * mm, "end": v(-10.81, -8.57) * mm});
            skLineSegment(sketch, "E635", {"start": v(-10.81, -8.57) * mm, "end": v(-10.12, -8.57) * mm});
            skLineSegment(sketch, "E636", {"start": v(-10.12, -8.57) * mm, "end": v(-9.5, -8.56) * mm});
            skLineSegment(sketch, "E637", {"start": v(-9.5, -8.56) * mm, "end": v(-8.78, -8.54) * mm});
            skLineSegment(sketch, "E638", {"start": v(-8.78, -8.54) * mm, "end": v(-8, -8.52) * mm});
            skLineSegment(sketch, "E639", {"start": v(-8, -8.52) * mm, "end": v(-7.17, -8.5) * mm});
            skLineSegment(sketch, "E640", {"start": v(-7.17, -8.5) * mm, "end": v(-6.36, -8.5) * mm});
            skLineSegment(sketch, "E641", {"start": v(-6.36, -8.5) * mm, "end": v(-5.6, -8.52) * mm});
            skLineSegment(sketch, "E642", {"start": v(-5.6, -8.52) * mm, "end": v(-4.95, -8.56) * mm});
            skLineSegment(sketch, "E643", {"start": v(-4.95, -8.56) * mm, "end": v(-4.42, -8.64) * mm});
            skLineSegment(sketch, "E644", {"start": v(-57.28, -14.94) * mm, "end": v(-57.28, -15.45) * mm});
            skLineSegment(sketch, "E645", {"start": v(-57.28, -15.45) * mm, "end": v(-56.07, -15.52) * mm});
            skLineSegment(sketch, "E646", {"start": v(-56.07, -15.52) * mm, "end": v(-53.5, -15.54) * mm});
            skLineSegment(sketch, "E647", {"start": v(-53.5, -15.54) * mm, "end": v(-50, -15.52) * mm});
            skLineSegment(sketch, "E648", {"start": v(-50, -15.52) * mm, "end": v(-45.99, -15.47) * mm});
            skLineSegment(sketch, "E649", {"start": v(-45.99, -15.47) * mm, "end": v(-41.88, -15.41) * mm});
            skLineSegment(sketch, "E650", {"start": v(-41.88, -15.41) * mm, "end": v(-38.12, -15.36) * mm});
            skLineSegment(sketch, "E651", {"start": v(-38.12, -15.36) * mm, "end": v(-35.11, -15.3) * mm});
            skLineSegment(sketch, "E652", {"start": v(-35.11, -15.3) * mm, "end": v(-33.29, -15.29) * mm});
            skLineSegment(sketch, "E653", {"start": v(-33.29, -15.29) * mm, "end": v(-32.6, -15.27) * mm});
            skLineSegment(sketch, "E654", {"start": v(-32.6, -15.27) * mm, "end": v(-31.93, -15.22) * mm});
            skLineSegment(sketch, "E655", {"start": v(-31.93, -15.22) * mm, "end": v(-31.27, -15.14) * mm});
            skLineSegment(sketch, "E656", {"start": v(-31.27, -15.14) * mm, "end": v(-30.64, -15.02) * mm});
            skLineSegment(sketch, "E657", {"start": v(-30.64, -15.02) * mm, "end": v(-30.04, -14.86) * mm});
            skLineSegment(sketch, "E658", {"start": v(-30.04, -14.86) * mm, "end": v(-29.49, -14.64) * mm});
            skLineSegment(sketch, "E659", {"start": v(-29.49, -14.64) * mm, "end": v(-29, -14.37) * mm});
            skLineSegment(sketch, "E660", {"start": v(-29, -14.37) * mm, "end": v(-28.56, -14.04) * mm});
            skLineSegment(sketch, "E661", {"start": v(-28.56, -14.04) * mm, "end": v(-28.1, -13.5) * mm});
            skLineSegment(sketch, "E662", {"start": v(-28.1, -13.5) * mm, "end": v(-27.91, -12.95) * mm});
            skLineSegment(sketch, "E663", {"start": v(-27.91, -12.95) * mm, "end": v(-27.93, -12.43) * mm});
            skLineSegment(sketch, "E664", {"start": v(-27.93, -12.43) * mm, "end": v(-28.13, -11.93) * mm});
            skLineSegment(sketch, "E665", {"start": v(-28.13, -11.93) * mm, "end": v(-28.46, -11.47) * mm});
            skLineSegment(sketch, "E666", {"start": v(-28.46, -11.47) * mm, "end": v(-28.9, -11.07) * mm});
            skLineSegment(sketch, "E667", {"start": v(-28.9, -11.07) * mm, "end": v(-29.41, -10.74) * mm});
            skLineSegment(sketch, "E668", {"start": v(-29.41, -10.74) * mm, "end": v(-29.95, -10.5) * mm});
            skLineSegment(sketch, "E669", {"start": v(-29.95, -10.5) * mm, "end": v(-30.9, -10.22) * mm});
            skLineSegment(sketch, "E670", {"start": v(-30.9, -10.22) * mm, "end": v(-32.2, -9.92) * mm});
            skLineSegment(sketch, "E671", {"start": v(-32.2, -9.92) * mm, "end": v(-33.72, -9.6) * mm});
            skLineSegment(sketch, "E672", {"start": v(-33.72, -9.6) * mm, "end": v(-35.31, -9.28) * mm});
            skLineSegment(sketch, "E673", {"start": v(-35.31, -9.28) * mm, "end": v(-36.84, -8.96) * mm});
            skLineSegment(sketch, "E674", {"start": v(-36.84, -8.96) * mm, "end": v(-38.16, -8.65) * mm});
            skLineSegment(sketch, "E675", {"start": v(-38.16, -8.65) * mm, "end": v(-39.16, -8.37) * mm});
            skLineSegment(sketch, "E676", {"start": v(-39.16, -8.37) * mm, "end": v(-39.68, -8.13) * mm});
            skLineSegment(sketch, "E677", {"start": v(-39.68, -8.13) * mm, "end": v(-37.79, -8.08) * mm});
            skLineSegment(sketch, "E678", {"start": v(-37.79, -8.08) * mm, "end": v(-35.88, -8.05) * mm});
            skLineSegment(sketch, "E679", {"start": v(-35.88, -8.05) * mm, "end": v(-33.96, -8.04) * mm});
            skLineSegment(sketch, "E680", {"start": v(-33.96, -8.04) * mm, "end": v(-32.05, -8.04) * mm});
            skLineSegment(sketch, "E681", {"start": v(-32.05, -8.04) * mm, "end": v(-30.13, -8.04) * mm});
            skLineSegment(sketch, "E682", {"start": v(-30.13, -8.04) * mm, "end": v(-28.23, -8.03) * mm});
            skLineSegment(sketch, "E683", {"start": v(-28.23, -8.03) * mm, "end": v(-26.35, -8) * mm});
            skLineSegment(sketch, "E684", {"start": v(-26.35, -8) * mm, "end": v(-24.5, -7.96) * mm});
            skLineSegment(sketch, "E685", {"start": v(-24.5, -7.96) * mm, "end": v(-24.16, -7.95) * mm});
            skLineSegment(sketch, "E686", {"start": v(-24.16, -7.95) * mm, "end": v(-23.9, -7.92) * mm});
            skLineSegment(sketch, "E687", {"start": v(-23.9, -7.92) * mm, "end": v(-23.68, -7.87) * mm});
            skLineSegment(sketch, "E688", {"start": v(-23.68, -7.87) * mm, "end": v(-23.5, -7.8) * mm});
            skLineSegment(sketch, "E689", {"start": v(-23.5, -7.8) * mm, "end": v(-23.35, -7.7) * mm});
            skLineSegment(sketch, "E690", {"start": v(-23.35, -7.7) * mm, "end": v(-23.2, -7.59) * mm});
            skLineSegment(sketch, "E691", {"start": v(-23.2, -7.59) * mm, "end": v(-23.03, -7.43) * mm});
            skLineSegment(sketch, "E692", {"start": v(-23.03, -7.43) * mm, "end": v(-22.84, -7.24) * mm});
            skLineSegment(sketch, "E693", {"start": v(-22.84, -7.24) * mm, "end": v(-22.53, -6.96) * mm});
            skLineSegment(sketch, "E694", {"start": v(-22.53, -6.96) * mm, "end": v(-22.18, -6.63) * mm});
            skLineSegment(sketch, "E695", {"start": v(-22.18, -6.63) * mm, "end": v(-22.01, -6.46) * mm});
            skLineSegment(sketch, "E696", {"start": v(-22.01, -6.46) * mm, "end": v(-21.87, -6.28) * mm});
            skLineSegment(sketch, "E697", {"start": v(-21.87, -6.28) * mm, "end": v(-21.76, -6.1) * mm});
            skLineSegment(sketch, "E698", {"start": v(-21.76, -6.1) * mm, "end": v(-21.7, -5.94) * mm});
            skLineSegment(sketch, "E699", {"start": v(-21.7, -5.94) * mm, "end": v(-22.9, -5.86) * mm});
            skLineSegment(sketch, "E700", {"start": v(-22.9, -5.86) * mm, "end": v(-25.32, -5.84) * mm});
            skLineSegment(sketch, "E701", {"start": v(-25.32, -5.84) * mm, "end": v(-28.6, -5.86) * mm});
            skLineSegment(sketch, "E702", {"start": v(-28.6, -5.86) * mm, "end": v(-32.32, -5.9) * mm});
            skLineSegment(sketch, "E703", {"start": v(-32.32, -5.9) * mm, "end": v(-36.14, -5.96) * mm});
            skLineSegment(sketch, "E704", {"start": v(-36.14, -5.96) * mm, "end": v(-39.64, -6.01) * mm});
            skLineSegment(sketch, "E705", {"start": v(-39.64, -6.01) * mm, "end": v(-42.47, -6.06) * mm});
            skLineSegment(sketch, "E706", {"start": v(-42.47, -6.06) * mm, "end": v(-44.23, -6.09) * mm});
            skLineSegment(sketch, "E707", {"start": v(-44.23, -6.09) * mm, "end": v(-46.04, -6.23) * mm});
            skLineSegment(sketch, "E708", {"start": v(-46.04, -6.23) * mm, "end": v(-47.44, -6.61) * mm});
            skLineSegment(sketch, "E709", {"start": v(-47.44, -6.61) * mm, "end": v(-48.43, -7.17) * mm});
            skLineSegment(sketch, "E710", {"start": v(-48.43, -7.17) * mm, "end": v(-49.03, -7.85) * mm});
            skLineSegment(sketch, "E711", {"start": v(-49.03, -7.85) * mm, "end": v(-49.23, -8.6) * mm});
            skLineSegment(sketch, "E712", {"start": v(-49.23, -8.6) * mm, "end": v(-49.05, -9.37) * mm});
            skLineSegment(sketch, "E713", {"start": v(-49.05, -9.37) * mm, "end": v(-48.5, -10.1) * mm});
            skLineSegment(sketch, "E714", {"start": v(-48.5, -10.1) * mm, "end": v(-47.57, -10.75) * mm});
            skLineSegment(sketch, "E715", {"start": v(-47.57, -10.75) * mm, "end": v(-47.1, -10.97) * mm});
            skLineSegment(sketch, "E716", {"start": v(-47.1, -10.97) * mm, "end": v(-46.57, -11.16) * mm});
            skLineSegment(sketch, "E717", {"start": v(-46.57, -11.16) * mm, "end": v(-46.02, -11.32) * mm});
            skLineSegment(sketch, "E718", {"start": v(-46.02, -11.32) * mm, "end": v(-45.45, -11.46) * mm});
            skLineSegment(sketch, "E719", {"start": v(-45.45, -11.46) * mm, "end": v(-44.87, -11.6) * mm});
            skLineSegment(sketch, "E720", {"start": v(-44.87, -11.6) * mm, "end": v(-44.28, -11.7) * mm});
            skLineSegment(sketch, "E721", {"start": v(-44.28, -11.7) * mm, "end": v(-43.71, -11.83) * mm});
            skLineSegment(sketch, "E722", {"start": v(-43.71, -11.83) * mm, "end": v(-43.16, -11.94) * mm});
            skLineSegment(sketch, "E723", {"start": v(-43.16, -11.94) * mm, "end": v(-42.81, -12.02) * mm});
            skLineSegment(sketch, "E724", {"start": v(-42.81, -12.02) * mm, "end": v(-42.27, -12.12) * mm});
            skLineSegment(sketch, "E725", {"start": v(-42.27, -12.12) * mm, "end": v(-41.6, -12.26) * mm});
            skLineSegment(sketch, "E726", {"start": v(-41.6, -12.26) * mm, "end": v(-40.87, -12.41) * mm});
            skLineSegment(sketch, "E727", {"start": v(-40.87, -12.41) * mm, "end": v(-40.14, -12.58) * mm});
            skLineSegment(sketch, "E728", {"start": v(-40.14, -12.58) * mm, "end": v(-39.5, -12.75) * mm});
            skLineSegment(sketch, "E729", {"start": v(-39.5, -12.75) * mm, "end": v(-38.99, -12.91) * mm});
            skLineSegment(sketch, "E730", {"start": v(-38.99, -12.91) * mm, "end": v(-38.69, -13.06) * mm});
            skLineSegment(sketch, "E731", {"start": v(-38.69, -13.06) * mm, "end": v(-39.4, -13.14) * mm});
            skLineSegment(sketch, "E732", {"start": v(-39.4, -13.14) * mm, "end": v(-40.93, -13.2) * mm});
            skLineSegment(sketch, "E733", {"start": v(-40.93, -13.2) * mm, "end": v(-43.05, -13.23) * mm});
            skLineSegment(sketch, "E734", {"start": v(-43.05, -13.23) * mm, "end": v(-45.5, -13.26) * mm});
            skLineSegment(sketch, "E735", {"start": v(-45.5, -13.26) * mm, "end": v(-48.04, -13.28) * mm});
            skLineSegment(sketch, "E736", {"start": v(-48.04, -13.28) * mm, "end": v(-50.4, -13.29) * mm});
            skLineSegment(sketch, "E737", {"start": v(-50.4, -13.29) * mm, "end": v(-52.35, -13.3) * mm});
            skLineSegment(sketch, "E738", {"start": v(-52.35, -13.3) * mm, "end": v(-53.63, -13.3) * mm});
            skLineSegment(sketch, "E739", {"start": v(-53.63, -13.3) * mm, "end": v(-54.66, -13.34) * mm});
            skLineSegment(sketch, "E740", {"start": v(-54.66, -13.34) * mm, "end": v(-55.35, -13.43) * mm});
            skLineSegment(sketch, "E741", {"start": v(-55.35, -13.43) * mm, "end": v(-55.78, -13.58) * mm});
            skLineSegment(sketch, "E742", {"start": v(-55.78, -13.58) * mm, "end": v(-56.06, -13.78) * mm});
            skLineSegment(sketch, "E743", {"start": v(-56.06, -13.78) * mm, "end": v(-56.26, -14.02) * mm});
            skLineSegment(sketch, "E744", {"start": v(-56.26, -14.02) * mm, "end": v(-56.47, -14.3) * mm});
            skLineSegment(sketch, "E745", {"start": v(-56.47, -14.3) * mm, "end": v(-56.78, -14.6) * mm});
            skLineSegment(sketch, "E746", {"start": v(-56.78, -14.6) * mm, "end": v(-57.28, -14.94) * mm});
            skLineSegment(sketch, "E747", {"start": v(57.28, 2.48) * mm, "end": v(56.87, 1.74) * mm});
            skLineSegment(sketch, "E748", {"start": v(56.87, 1.74) * mm, "end": v(56.69, 0.86) * mm});
            skLineSegment(sketch, "E749", {"start": v(56.69, 0.86) * mm, "end": v(56.67, -0.13) * mm});
            skLineSegment(sketch, "E750", {"start": v(56.67, -0.13) * mm, "end": v(56.75, -1.2) * mm});
            skLineSegment(sketch, "E751", {"start": v(56.75, -1.2) * mm, "end": v(56.86, -2.33) * mm});
            skLineSegment(sketch, "E752", {"start": v(56.86, -2.33) * mm, "end": v(56.93, -3.46) * mm});
            skLineSegment(sketch, "E753", {"start": v(56.93, -3.46) * mm, "end": v(56.89, -4.58) * mm});
            skLineSegment(sketch, "E754", {"start": v(56.89, -4.58) * mm, "end": v(56.66, -5.65) * mm});
            skLineSegment(sketch, "E755", {"start": v(56.66, -5.65) * mm, "end": v(56.37, -6.35) * mm});
            skLineSegment(sketch, "E756", {"start": v(56.37, -6.35) * mm, "end": v(55.94, -7.1) * mm});
            skLineSegment(sketch, "E757", {"start": v(55.94, -7.1) * mm, "end": v(55.42, -7.88) * mm});
            skLineSegment(sketch, "E758", {"start": v(55.42, -7.88) * mm, "end": v(54.83, -8.63) * mm});
            skLineSegment(sketch, "E759", {"start": v(54.83, -8.63) * mm, "end": v(54.22, -9.33) * mm});
            skLineSegment(sketch, "E760", {"start": v(54.22, -9.33) * mm, "end": v(53.61, -9.95) * mm});
            skLineSegment(sketch, "E761", {"start": v(53.61, -9.95) * mm, "end": v(53.05, -10.44) * mm});
            skLineSegment(sketch, "E762", {"start": v(53.05, -10.44) * mm, "end": v(52.56, -10.77) * mm});
            skLineSegment(sketch, "E763", {"start": v(52.56, -10.77) * mm, "end": v(52.56, -10.35) * mm});
            skLineSegment(sketch, "E764", {"start": v(52.56, -10.35) * mm, "end": v(52.57, -9.85) * mm});
            skLineSegment(sketch, "E765", {"start": v(52.57, -9.85) * mm, "end": v(52.6, -9.36) * mm});
            skLineSegment(sketch, "E766", {"start": v(52.6, -9.36) * mm, "end": v(52.66, -8.97) * mm});
            skLineSegment(sketch, "E767", {"start": v(52.66, -8.97) * mm, "end": v(52.74, -8.72) * mm});
            skLineSegment(sketch, "E768", {"start": v(52.74, -8.72) * mm, "end": v(52.83, -8.54) * mm});
            skLineSegment(sketch, "E769", {"start": v(52.83, -8.54) * mm, "end": v(52.94, -8.42) * mm});
            skLineSegment(sketch, "E770", {"start": v(52.94, -8.42) * mm, "end": v(53.06, -8.32) * mm});
            skLineSegment(sketch, "E771", {"start": v(53.06, -8.32) * mm, "end": v(53.19, -8.24) * mm});
            skLineSegment(sketch, "E772", {"start": v(53.19, -8.24) * mm, "end": v(53.32, -8.13) * mm});
            skLineSegment(sketch, "E773", {"start": v(53.32, -8.13) * mm, "end": v(53.46, -7.99) * mm});
            skLineSegment(sketch, "E774", {"start": v(53.46, -7.99) * mm, "end": v(53.6, -7.78) * mm});
            skLineSegment(sketch, "E775", {"start": v(53.6, -7.78) * mm, "end": v(50.15, -7.77) * mm});
            skLineSegment(sketch, "E776", {"start": v(50.15, -7.77) * mm, "end": v(49.83, -8.25) * mm});
            skLineSegment(sketch, "E777", {"start": v(49.83, -8.25) * mm, "end": v(49.5, -8.65) * mm});
            skLineSegment(sketch, "E778", {"start": v(49.5, -8.65) * mm, "end": v(49.15, -8.99) * mm});
            skLineSegment(sketch, "E779", {"start": v(49.15, -8.99) * mm, "end": v(48.78, -9.3) * mm});
            skLineSegment(sketch, "E780", {"start": v(48.78, -9.3) * mm, "end": v(48.4, -9.58) * mm});
            skLineSegment(sketch, "E781", {"start": v(48.4, -9.58) * mm, "end": v(47.98, -9.86) * mm});
            skLineSegment(sketch, "E782", {"start": v(47.98, -9.86) * mm, "end": v(47.54, -10.15) * mm});
            skLineSegment(sketch, "E783", {"start": v(47.54, -10.15) * mm, "end": v(47.08, -10.48) * mm});
            skLineSegment(sketch, "E784", {"start": v(47.08, -10.48) * mm, "end": v(47.09, -10.25) * mm});
            skLineSegment(sketch, "E785", {"start": v(47.09, -10.25) * mm, "end": v(47.13, -9.95) * mm});
            skLineSegment(sketch, "E786", {"start": v(47.13, -9.95) * mm, "end": v(47.2, -9.6) * mm});
            skLineSegment(sketch, "E787", {"start": v(47.2, -9.6) * mm, "end": v(47.28, -9.23) * mm});
            skLineSegment(sketch, "E788", {"start": v(47.28, -9.23) * mm, "end": v(47.46, -8.5) * mm});
            skLineSegment(sketch, "E789", {"start": v(47.46, -8.5) * mm, "end": v(47.6, -7.94) * mm});
            skLineSegment(sketch, "E790", {"start": v(47.6, -7.94) * mm, "end": v(47.74, -7.49) * mm});
            skLineSegment(sketch, "E791", {"start": v(47.74, -7.49) * mm, "end": v(47.85, -7.2) * mm});
            skLineSegment(sketch, "E792", {"start": v(47.85, -7.2) * mm, "end": v(47.94, -7.02) * mm});
            skLineSegment(sketch, "E793", {"start": v(47.94, -7.02) * mm, "end": v(47.98, -6.9) * mm});
            skLineSegment(sketch, "E794", {"start": v(47.98, -6.9) * mm, "end": v(47.97, -6.8) * mm});
            skLineSegment(sketch, "E795", {"start": v(47.97, -6.8) * mm, "end": v(47.9, -6.64) * mm});
            skLineSegment(sketch, "E796", {"start": v(47.9, -6.64) * mm, "end": v(47.73, -6.38) * mm});
            skLineSegment(sketch, "E797", {"start": v(47.73, -6.38) * mm, "end": v(47.47, -5.97) * mm});
            skLineSegment(sketch, "E798", {"start": v(47.47, -5.97) * mm, "end": v(47.13, -6.16) * mm});
            skLineSegment(sketch, "E799", {"start": v(47.13, -6.16) * mm, "end": v(46.8, -6.44) * mm});
            skLineSegment(sketch, "E800", {"start": v(46.8, -6.44) * mm, "end": v(46.47, -6.73) * mm});
            skLineSegment(sketch, "E801", {"start": v(46.47, -6.73) * mm, "end": v(46.16, -6.98) * mm});
            skLineSegment(sketch, "E802", {"start": v(46.16, -6.98) * mm, "end": v(45.9, -7.12) * mm});
            skLineSegment(sketch, "E803", {"start": v(45.9, -7.12) * mm, "end": v(45.69, -7.1) * mm});
            skLineSegment(sketch, "E804", {"start": v(45.69, -7.1) * mm, "end": v(45.53, -6.85) * mm});
            skLineSegment(sketch, "E805", {"start": v(45.53, -6.85) * mm, "end": v(45.46, -6.32) * mm});
            skLineSegment(sketch, "E806", {"start": v(45.46, -6.32) * mm, "end": v(45.44, -5.71) * mm});
            skLineSegment(sketch, "E807", {"start": v(45.44, -5.71) * mm, "end": v(45.44, -5.3) * mm});
            skLineSegment(sketch, "E808", {"start": v(45.44, -5.3) * mm, "end": v(45.47, -5.05) * mm});
            skLineSegment(sketch, "E809", {"start": v(45.47, -5.05) * mm, "end": v(45.5, -4.9) * mm});
            skLineSegment(sketch, "E810", {"start": v(45.5, -4.9) * mm, "end": v(45.56, -4.83) * mm});
            skLineSegment(sketch, "E811", {"start": v(45.56, -4.83) * mm, "end": v(45.6, -4.77) * mm});
            skLineSegment(sketch, "E812", {"start": v(45.6, -4.77) * mm, "end": v(45.66, -4.7) * mm});
            skLineSegment(sketch, "E813", {"start": v(45.66, -4.7) * mm, "end": v(45.7, -4.55) * mm});
            skLineSegment(sketch, "E814", {"start": v(45.7, -4.55) * mm, "end": v(45.72, -4.35) * mm});
            skLineSegment(sketch, "E815", {"start": v(45.72, -4.35) * mm, "end": v(45.68, -4.19) * mm});
            skLineSegment(sketch, "E816", {"start": v(45.68, -4.19) * mm, "end": v(45.6, -4.04) * mm});
            skLineSegment(sketch, "E817", {"start": v(45.6, -4.04) * mm, "end": v(45.5, -3.9) * mm});
            skLineSegment(sketch, "E818", {"start": v(45.5, -3.9) * mm, "end": v(45.24, -3.66) * mm});
            skLineSegment(sketch, "E819", {"start": v(45.24, -3.66) * mm, "end": v(44.97, -3.39) * mm});
            skLineSegment(sketch, "E820", {"start": v(44.97, -3.39) * mm, "end": v(44.74, -3.8) * mm});
            skLineSegment(sketch, "E821", {"start": v(44.74, -3.8) * mm, "end": v(44.68, -3.9) * mm});
            skLineSegment(sketch, "E822", {"start": v(44.68, -3.9) * mm, "end": v(44.57, -4.04) * mm});
            skLineSegment(sketch, "E823", {"start": v(44.57, -4.04) * mm, "end": v(44.45, -4.16) * mm});
            skLineSegment(sketch, "E824", {"start": v(44.45, -4.16) * mm, "end": v(44.32, -4.26) * mm});
            skLineSegment(sketch, "E825", {"start": v(44.32, -4.26) * mm, "end": v(44.17, -4.34) * mm});
            skLineSegment(sketch, "E826", {"start": v(44.17, -4.34) * mm, "end": v(44.01, -4.4) * mm});
            skLineSegment(sketch, "E827", {"start": v(44.01, -4.4) * mm, "end": v(43.84, -4.44) * mm});
            skLineSegment(sketch, "E828", {"start": v(43.84, -4.44) * mm, "end": v(43.65, -4.47) * mm});
            skLineSegment(sketch, "E829", {"start": v(43.65, -4.47) * mm, "end": v(43.45, -4.48) * mm});
            skLineSegment(sketch, "E830", {"start": v(43.45, -4.48) * mm, "end": v(43.27, -3.83) * mm});
            skLineSegment(sketch, "E831", {"start": v(43.27, -3.83) * mm, "end": v(43.2, -3.26) * mm});
            skLineSegment(sketch, "E832", {"start": v(43.2, -3.26) * mm, "end": v(43.17, -2.77) * mm});
            skLineSegment(sketch, "E833", {"start": v(43.17, -2.77) * mm, "end": v(43.12, -2.35) * mm});
            skLineSegment(sketch, "E834", {"start": v(43.12, -2.35) * mm, "end": v(42.96, -1.98) * mm});
            skLineSegment(sketch, "E835", {"start": v(42.96, -1.98) * mm, "end": v(42.62, -1.66) * mm});
            skLineSegment(sketch, "E836", {"start": v(42.62, -1.66) * mm, "end": v(42.03, -1.38) * mm});
            skLineSegment(sketch, "E837", {"start": v(42.03, -1.38) * mm, "end": v(41.13, -1.13) * mm});
            skLineSegment(sketch, "E838", {"start": v(41.13, -1.13) * mm, "end": v(40.78, -1.06) * mm});
            skLineSegment(sketch, "E839", {"start": v(40.78, -1.06) * mm, "end": v(40.44, -1) * mm});
            skLineSegment(sketch, "E840", {"start": v(40.44, -1) * mm, "end": v(40.11, -0.96) * mm});
            skLineSegment(sketch, "E841", {"start": v(40.11, -0.96) * mm, "end": v(39.8, -0.96) * mm});
            skLineSegment(sketch, "E842", {"start": v(39.8, -0.96) * mm, "end": v(39.5, -1) * mm});
            skLineSegment(sketch, "E843", {"start": v(39.5, -1) * mm, "end": v(39.24, -1.08) * mm});
            skLineSegment(sketch, "E844", {"start": v(39.24, -1.08) * mm, "end": v(39, -1.22) * mm});
            skLineSegment(sketch, "E845", {"start": v(39, -1.22) * mm, "end": v(38.78, -1.43) * mm});
            skLineSegment(sketch, "E846", {"start": v(38.78, -1.43) * mm, "end": v(38.64, -1.6) * mm});
            skLineSegment(sketch, "E847", {"start": v(38.64, -1.6) * mm, "end": v(38.5, -1.82) * mm});
            skLineSegment(sketch, "E848", {"start": v(38.5, -1.82) * mm, "end": v(38.36, -2.05) * mm});
            skLineSegment(sketch, "E849", {"start": v(38.36, -2.05) * mm, "end": v(38.23, -2.3) * mm});
            skLineSegment(sketch, "E850", {"start": v(38.23, -2.3) * mm, "end": v(38.11, -2.56) * mm});
            skLineSegment(sketch, "E851", {"start": v(38.11, -2.56) * mm, "end": v(38.02, -2.82) * mm});
            skLineSegment(sketch, "E852", {"start": v(38.02, -2.82) * mm, "end": v(37.95, -3.08) * mm});
            skLineSegment(sketch, "E853", {"start": v(37.95, -3.08) * mm, "end": v(37.91, -3.32) * mm});
            skLineSegment(sketch, "E854", {"start": v(37.91, -3.32) * mm, "end": v(38.15, -3.5) * mm});
            skLineSegment(sketch, "E855", {"start": v(38.15, -3.5) * mm, "end": v(38.3, -3.6) * mm});
            skLineSegment(sketch, "E856", {"start": v(38.3, -3.6) * mm, "end": v(38.36, -3.65) * mm});
            skLineSegment(sketch, "E857", {"start": v(38.36, -3.65) * mm, "end": v(38.42, -3.71) * mm});
            skLineSegment(sketch, "E858", {"start": v(38.42, -3.71) * mm, "end": v(38.5, -3.8) * mm});
            skLineSegment(sketch, "E859", {"start": v(38.5, -3.8) * mm, "end": v(38.57, -3.92) * mm});
            skLineSegment(sketch, "E860", {"start": v(38.57, -3.92) * mm, "end": v(38.37, -4.13) * mm});
            skLineSegment(sketch, "E861", {"start": v(38.37, -4.13) * mm, "end": v(38.14, -4.36) * mm});
            skLineSegment(sketch, "E862", {"start": v(38.14, -4.36) * mm, "end": v(37.92, -4.6) * mm});
            skLineSegment(sketch, "E863", {"start": v(37.92, -4.6) * mm, "end": v(37.72, -4.86) * mm});
            skLineSegment(sketch, "E864", {"start": v(37.72, -4.86) * mm, "end": v(37.55, -5.17) * mm});
            skLineSegment(sketch, "E865", {"start": v(37.55, -5.17) * mm, "end": v(37.43, -5.51) * mm});
            skLineSegment(sketch, "E866", {"start": v(37.43, -5.51) * mm, "end": v(37.37, -5.9) * mm});
            skLineSegment(sketch, "E867", {"start": v(37.37, -5.9) * mm, "end": v(37.4, -6.36) * mm});
            skLineSegment(sketch, "E868", {"start": v(37.4, -6.36) * mm, "end": v(37.7, -6.57) * mm});
            skLineSegment(sketch, "E869", {"start": v(37.7, -6.57) * mm, "end": v(38, -6.74) * mm});
            skLineSegment(sketch, "E870", {"start": v(38, -6.74) * mm, "end": v(38.16, -6.82) * mm});
            skLineSegment(sketch, "E871", {"start": v(38.16, -6.82) * mm, "end": v(38.3, -6.9) * mm});
            skLineSegment(sketch, "E872", {"start": v(38.3, -6.9) * mm, "end": v(38.46, -7) * mm});
            skLineSegment(sketch, "E873", {"start": v(38.46, -7) * mm, "end": v(38.61, -7.13) * mm});
            skLineSegment(sketch, "E874", {"start": v(38.61, -7.13) * mm, "end": v(38.52, -7.31) * mm});
            skLineSegment(sketch, "E875", {"start": v(38.52, -7.31) * mm, "end": v(38.4, -7.47) * mm});
            skLineSegment(sketch, "E876", {"start": v(38.4, -7.47) * mm, "end": v(38.27, -7.6) * mm});
            skLineSegment(sketch, "E877", {"start": v(38.27, -7.6) * mm, "end": v(38.13, -7.73) * mm});
            skLineSegment(sketch, "E878", {"start": v(38.13, -7.73) * mm, "end": v(37.77, -8) * mm});
            skLineSegment(sketch, "E879", {"start": v(37.77, -8) * mm, "end": v(37.34, -8.3) * mm});
            skLineSegment(sketch, "E880", {"start": v(37.34, -8.3) * mm, "end": v(37.41, -9.41) * mm});
            skLineSegment(sketch, "E881", {"start": v(37.41, -9.41) * mm, "end": v(37.68, -10.08) * mm});
            skLineSegment(sketch, "E882", {"start": v(37.68, -10.08) * mm, "end": v(38.12, -10.38) * mm});
            skLineSegment(sketch, "E883", {"start": v(38.12, -10.38) * mm, "end": v(38.67, -10.37) * mm});
            skLineSegment(sketch, "E884", {"start": v(38.67, -10.37) * mm, "end": v(39.31, -10.13) * mm});
            skLineSegment(sketch, "E885", {"start": v(39.31, -10.13) * mm, "end": v(40, -9.71) * mm});
            skLineSegment(sketch, "E886", {"start": v(40, -9.71) * mm, "end": v(40.7, -9.2) * mm});
            skLineSegment(sketch, "E887", {"start": v(40.7, -9.2) * mm, "end": v(41.36, -8.65) * mm});
            skLineSegment(sketch, "E888", {"start": v(41.36, -8.65) * mm, "end": v(41.41, -9.14) * mm});
            skLineSegment(sketch, "E889", {"start": v(41.41, -9.14) * mm, "end": v(41.36, -9.55) * mm});
            skLineSegment(sketch, "E890", {"start": v(41.36, -9.55) * mm, "end": v(41.24, -9.9) * mm});
            skLineSegment(sketch, "E891", {"start": v(41.24, -9.9) * mm, "end": v(41.07, -10.2) * mm});
            skLineSegment(sketch, "E892", {"start": v(41.07, -10.2) * mm, "end": v(40.88, -10.5) * mm});
            skLineSegment(sketch, "E893", {"start": v(40.88, -10.5) * mm, "end": v(40.7, -10.78) * mm});
            skLineSegment(sketch, "E894", {"start": v(40.7, -10.78) * mm, "end": v(40.54, -11.1) * mm});
            skLineSegment(sketch, "E895", {"start": v(40.54, -11.1) * mm, "end": v(40.45, -11.46) * mm});
            skLineSegment(sketch, "E896", {"start": v(40.45, -11.46) * mm, "end": v(42.64, -11.82) * mm});
            skLineSegment(sketch, "E897", {"start": v(42.64, -11.82) * mm, "end": v(42.44, -11.63) * mm});
            skLineSegment(sketch, "E898", {"start": v(42.44, -11.63) * mm, "end": v(42.28, -11.46) * mm});
            skLineSegment(sketch, "E899", {"start": v(42.28, -11.46) * mm, "end": v(42.14, -11.3) * mm});
            skLineSegment(sketch, "E900", {"start": v(42.14, -11.3) * mm, "end": v(42.02, -11.15) * mm});
            skLineSegment(sketch, "E901", {"start": v(42.02, -11.15) * mm, "end": v(41.92, -10.97) * mm});
            skLineSegment(sketch, "E902", {"start": v(41.92, -10.97) * mm, "end": v(41.85, -10.75) * mm});
            skLineSegment(sketch, "E903", {"start": v(41.85, -10.75) * mm, "end": v(41.78, -10.49) * mm});
            skLineSegment(sketch, "E904", {"start": v(41.78, -10.49) * mm, "end": v(41.73, -10.15) * mm});
            skLineSegment(sketch, "E905", {"start": v(41.73, -10.15) * mm, "end": v(41.64, -9.35) * mm});
            skLineSegment(sketch, "E906", {"start": v(41.64, -9.35) * mm, "end": v(41.6, -8.5) * mm});
            skLineSegment(sketch, "E907", {"start": v(41.6, -8.5) * mm, "end": v(41.6, -7.6) * mm});
            skLineSegment(sketch, "E908", {"start": v(41.6, -7.6) * mm, "end": v(41.68, -6.72) * mm});
            skLineSegment(sketch, "E909", {"start": v(41.68, -6.72) * mm, "end": v(41.84, -5.87) * mm});
            skLineSegment(sketch, "E910", {"start": v(41.84, -5.87) * mm, "end": v(42.09, -5.08) * mm});
            skLineSegment(sketch, "E911", {"start": v(42.09, -5.08) * mm, "end": v(42.45, -4.38) * mm});
            skLineSegment(sketch, "E912", {"start": v(42.45, -4.38) * mm, "end": v(42.92, -3.8) * mm});
            skLineSegment(sketch, "E913", {"start": v(42.92, -3.8) * mm, "end": v(42.9, -4.08) * mm});
            skLineSegment(sketch, "E914", {"start": v(42.9, -4.08) * mm, "end": v(42.83, -4.3) * mm});
            skLineSegment(sketch, "E915", {"start": v(42.83, -4.3) * mm, "end": v(42.77, -4.5) * mm});
            skLineSegment(sketch, "E916", {"start": v(42.77, -4.5) * mm, "end": v(42.74, -4.67) * mm});
            skLineSegment(sketch, "E917", {"start": v(42.74, -4.67) * mm, "end": v(42.75, -4.82) * mm});
            skLineSegment(sketch, "E918", {"start": v(42.75, -4.82) * mm, "end": v(42.77, -4.95) * mm});
            skLineSegment(sketch, "E919", {"start": v(42.77, -4.95) * mm, "end": v(42.81, -5.05) * mm});
            skLineSegment(sketch, "E920", {"start": v(42.81, -5.05) * mm, "end": v(42.86, -5.14) * mm});
            skLineSegment(sketch, "E921", {"start": v(42.86, -5.14) * mm, "end": v(42.97, -5.3) * mm});
            skLineSegment(sketch, "E922", {"start": v(42.97, -5.3) * mm, "end": v(43.06, -5.47) * mm});
            skLineSegment(sketch, "E923", {"start": v(43.06, -5.47) * mm, "end": v(42.86, -5.64) * mm});
            skLineSegment(sketch, "E924", {"start": v(42.86, -5.64) * mm, "end": v(42.68, -5.89) * mm});
            skLineSegment(sketch, "E925", {"start": v(42.68, -5.89) * mm, "end": v(42.53, -6.18) * mm});
            skLineSegment(sketch, "E926", {"start": v(42.53, -6.18) * mm, "end": v(42.42, -6.5) * mm});
            skLineSegment(sketch, "E927", {"start": v(42.42, -6.5) * mm, "end": v(42.35, -6.83) * mm});
            skLineSegment(sketch, "E928", {"start": v(42.35, -6.83) * mm, "end": v(42.34, -7.16) * mm});
            skLineSegment(sketch, "E929", {"start": v(42.34, -7.16) * mm, "end": v(42.4, -7.47) * mm});
            skLineSegment(sketch, "E930", {"start": v(42.4, -7.47) * mm, "end": v(42.52, -7.74) * mm});
            skLineSegment(sketch, "E931", {"start": v(42.52, -7.74) * mm, "end": v(43, -8.16) * mm});
            skLineSegment(sketch, "E932", {"start": v(43, -8.16) * mm, "end": v(42.86, -8.61) * mm});
            skLineSegment(sketch, "E933", {"start": v(42.86, -8.61) * mm, "end": v(42.79, -9.04) * mm});
            skLineSegment(sketch, "E934", {"start": v(42.79, -9.04) * mm, "end": v(42.77, -9.44) * mm});
            skLineSegment(sketch, "E935", {"start": v(42.77, -9.44) * mm, "end": v(42.83, -9.81) * mm});
            skLineSegment(sketch, "E936", {"start": v(42.83, -9.81) * mm, "end": v(42.94, -10.16) * mm});
            skLineSegment(sketch, "E937", {"start": v(42.94, -10.16) * mm, "end": v(43.12, -10.48) * mm});
            skLineSegment(sketch, "E938", {"start": v(43.12, -10.48) * mm, "end": v(43.36, -10.77) * mm});
            skLineSegment(sketch, "E939", {"start": v(43.36, -10.77) * mm, "end": v(43.67, -11.04) * mm});
            skLineSegment(sketch, "E940", {"start": v(43.67, -11.04) * mm, "end": v(44.1, -11) * mm});
            skLineSegment(sketch, "E941", {"start": v(44.1, -11) * mm, "end": v(44.42, -10.88) * mm});
            skLineSegment(sketch, "E942", {"start": v(44.42, -10.88) * mm, "end": v(44.65, -10.7) * mm});
            skLineSegment(sketch, "E943", {"start": v(44.65, -10.7) * mm, "end": v(44.84, -10.5) * mm});
            skLineSegment(sketch, "E944", {"start": v(44.84, -10.5) * mm, "end": v(45, -10.27) * mm});
            skLineSegment(sketch, "E945", {"start": v(45, -10.27) * mm, "end": v(45.15, -10.05) * mm});
            skLineSegment(sketch, "E946", {"start": v(45.15, -10.05) * mm, "end": v(45.33, -9.86) * mm});
            skLineSegment(sketch, "E947", {"start": v(45.33, -9.86) * mm, "end": v(45.57, -9.7) * mm});
            skLineSegment(sketch, "E948", {"start": v(45.57, -9.7) * mm, "end": v(45.42, -11.6) * mm});
            skLineSegment(sketch, "E949", {"start": v(45.42, -11.6) * mm, "end": v(44.75, -13.04) * mm});
            skLineSegment(sketch, "E950", {"start": v(44.75, -13.04) * mm, "end": v(43.73, -14.08) * mm});
            skLineSegment(sketch, "E951", {"start": v(43.73, -14.08) * mm, "end": v(42.49, -14.8) * mm});
            skLineSegment(sketch, "E952", {"start": v(42.49, -14.8) * mm, "end": v(41.18, -15.27) * mm});
            skLineSegment(sketch, "E953", {"start": v(41.18, -15.27) * mm, "end": v(39.95, -15.58) * mm});
            skLineSegment(sketch, "E954", {"start": v(39.95, -15.58) * mm, "end": v(38.94, -15.8) * mm});
            skLineSegment(sketch, "E955", {"start": v(38.94, -15.8) * mm, "end": v(38.3, -16) * mm});
            skLineSegment(sketch, "E956", {"start": v(30.52, 19.83) * mm, "end": v(30.81, 19.7) * mm});
            skLineSegment(sketch, "E957", {"start": v(30.81, 19.7) * mm, "end": v(31.14, 19.58) * mm});
            skLineSegment(sketch, "E958", {"start": v(31.14, 19.58) * mm, "end": v(31.5, 19.49) * mm});
            skLineSegment(sketch, "E959", {"start": v(31.5, 19.49) * mm, "end": v(31.86, 19.4) * mm});
            skLineSegment(sketch, "E960", {"start": v(31.86, 19.4) * mm, "end": v(32.6, 19.26) * mm});
            skLineSegment(sketch, "E961", {"start": v(32.6, 19.26) * mm, "end": v(33.3, 19.09) * mm});
            skLineSegment(sketch, "E962", {"start": v(33.3, 19.09) * mm, "end": v(34.37, 18.72) * mm});
            skLineSegment(sketch, "E963", {"start": v(34.37, 18.72) * mm, "end": v(35.48, 18.3) * mm});
            skLineSegment(sketch, "E964", {"start": v(35.48, 18.3) * mm, "end": v(36.6, 17.85) * mm});
            skLineSegment(sketch, "E965", {"start": v(36.6, 17.85) * mm, "end": v(37.71, 17.41) * mm});
            skLineSegment(sketch, "E966", {"start": v(37.71, 17.41) * mm, "end": v(38.78, 17) * mm});
            skLineSegment(sketch, "E967", {"start": v(38.78, 17) * mm, "end": v(39.78, 16.65) * mm});
            skLineSegment(sketch, "E968", {"start": v(39.78, 16.65) * mm, "end": v(40.69, 16.4) * mm});
            skLineSegment(sketch, "E969", {"start": v(40.69, 16.4) * mm, "end": v(41.49, 16.25) * mm});
            skLineSegment(sketch, "E970", {"start": v(41.49, 16.25) * mm, "end": v(41.03, 18.26) * mm});
            skLineSegment(sketch, "E971", {"start": v(41.03, 18.26) * mm, "end": v(42.02, 17.96) * mm});
            skLineSegment(sketch, "E972", {"start": v(42.02, 17.96) * mm, "end": v(43.23, 17.42) * mm});
            skLineSegment(sketch, "E973", {"start": v(43.23, 17.42) * mm, "end": v(44.57, 16.7) * mm});
            skLineSegment(sketch, "E974", {"start": v(44.57, 16.7) * mm, "end": v(45.98, 15.86) * mm});
            skLineSegment(sketch, "E975", {"start": v(45.98, 15.86) * mm, "end": v(47.37, 14.98) * mm});
            skLineSegment(sketch, "E976", {"start": v(47.37, 14.98) * mm, "end": v(48.66, 14.12) * mm});
            skLineSegment(sketch, "E977", {"start": v(48.66, 14.12) * mm, "end": v(49.77, 13.35) * mm});
            skLineSegment(sketch, "E978", {"start": v(49.77, 13.35) * mm, "end": v(50.63, 12.72) * mm});
            skLineSegment(sketch, "E979", {"start": v(50.63, 12.72) * mm, "end": v(51.36, 12.14) * mm});
            skLineSegment(sketch, "E980", {"start": v(51.36, 12.14) * mm, "end": v(52.12, 11.47) * mm});
            skLineSegment(sketch, "E981", {"start": v(52.12, 11.47) * mm, "end": v(52.87, 10.74) * mm});
            skLineSegment(sketch, "E982", {"start": v(52.87, 10.74) * mm, "end": v(53.61, 9.96) * mm});
            skLineSegment(sketch, "E983", {"start": v(53.61, 9.96) * mm, "end": v(54.32, 9.14) * mm});
            skLineSegment(sketch, "E984", {"start": v(54.32, 9.14) * mm, "end": v(54.97, 8.31) * mm});
            skLineSegment(sketch, "E985", {"start": v(54.97, 8.31) * mm, "end": v(55.55, 7.48) * mm});
            skLineSegment(sketch, "E986", {"start": v(55.55, 7.48) * mm, "end": v(56.04, 6.67) * mm});
            skLineSegment(sketch, "E987", {"start": v(56.04, 6.67) * mm, "end": v(56.2, 6.34) * mm});
            skLineSegment(sketch, "E988", {"start": v(56.2, 6.34) * mm, "end": v(56.36, 6) * mm});
            skLineSegment(sketch, "E989", {"start": v(56.36, 6) * mm, "end": v(56.5, 5.65) * mm});
            skLineSegment(sketch, "E990", {"start": v(56.5, 5.65) * mm, "end": v(56.63, 5.3) * mm});
            skLineSegment(sketch, "E991", {"start": v(56.63, 5.3) * mm, "end": v(56.77, 4.95) * mm});
            skLineSegment(sketch, "E992", {"start": v(56.77, 4.95) * mm, "end": v(56.92, 4.62) * mm});
            skLineSegment(sketch, "E993", {"start": v(56.92, 4.62) * mm, "end": v(57.08, 4.3) * mm});
            skLineSegment(sketch, "E994", {"start": v(57.08, 4.3) * mm, "end": v(57.26, 4) * mm});
            skLineSegment(sketch, "E995", {"start": v(3.98, -8.38) * mm, "end": v(14, -8.35) * mm});
            skLineSegment(sketch, "E996", {"start": v(14, -8.35) * mm, "end": v(13.73, -8.7) * mm});
            skLineSegment(sketch, "E997", {"start": v(13.73, -8.7) * mm, "end": v(13.24, -9.26) * mm});
            skLineSegment(sketch, "E998", {"start": v(13.24, -9.26) * mm, "end": v(12.6, -9.95) * mm});
            skLineSegment(sketch, "E999", {"start": v(12.6, -9.95) * mm, "end": v(11.85, -10.7) * mm});
            skLineSegment(sketch, "E1000", {"start": v(11.85, -10.7) * mm, "end": v(11.07, -11.48) * mm});
            skLineSegment(sketch, "E1001", {"start": v(11.07, -11.48) * mm, "end": v(10.34, -12.22) * mm});
            skLineSegment(sketch, "E1002", {"start": v(10.34, -12.22) * mm, "end": v(9.7, -12.85) * mm});
            skLineSegment(sketch, "E1003", {"start": v(9.7, -12.85) * mm, "end": v(9.25, -13.33) * mm});
            skLineSegment(sketch, "E1004", {"start": v(9.25, -13.33) * mm, "end": v(8.62, -13.95) * mm});
            skLineSegment(sketch, "E1005", {"start": v(8.62, -13.95) * mm, "end": v(8.17, -14.39) * mm});
            skLineSegment(sketch, "E1006", {"start": v(8.17, -14.39) * mm, "end": v(8.02, -14.57) * mm});
            skLineSegment(sketch, "E1007", {"start": v(8.02, -14.57) * mm, "end": v(7.93, -14.75) * mm});
            skLineSegment(sketch, "E1008", {"start": v(7.93, -14.75) * mm, "end": v(7.9, -14.93) * mm});
            skLineSegment(sketch, "E1009", {"start": v(7.9, -14.93) * mm, "end": v(7.95, -15.13) * mm});
            skLineSegment(sketch, "E1010", {"start": v(7.95, -15.13) * mm, "end": v(8.33, -15.24) * mm});
            skLineSegment(sketch, "E1011", {"start": v(8.33, -15.24) * mm, "end": v(8.77, -15.3) * mm});
            skLineSegment(sketch, "E1012", {"start": v(8.77, -15.3) * mm, "end": v(9.26, -15.32) * mm});
            skLineSegment(sketch, "E1013", {"start": v(9.26, -15.32) * mm, "end": v(9.79, -15.31) * mm});
            skLineSegment(sketch, "E1014", {"start": v(9.79, -15.31) * mm, "end": v(10.32, -15.28) * mm});
            skLineSegment(sketch, "E1015", {"start": v(10.32, -15.28) * mm, "end": v(10.85, -15.25) * mm});
            skLineSegment(sketch, "E1016", {"start": v(10.85, -15.25) * mm, "end": v(11.34, -15.22) * mm});
            skLineSegment(sketch, "E1017", {"start": v(11.34, -15.22) * mm, "end": v(11.8, -15.2) * mm});
            skLineSegment(sketch, "E1018", {"start": v(11.8, -15.2) * mm, "end": v(12.31, -15.2) * mm});
            skLineSegment(sketch, "E1019", {"start": v(12.31, -15.2) * mm, "end": v(12.8, -15.22) * mm});
            skLineSegment(sketch, "E1020", {"start": v(12.8, -15.22) * mm, "end": v(13.26, -15.23) * mm});
            skLineSegment(sketch, "E1021", {"start": v(13.26, -15.23) * mm, "end": v(13.69, -15.2) * mm});
            skLineSegment(sketch, "E1022", {"start": v(13.69, -15.2) * mm, "end": v(14.09, -15.15) * mm});
            skLineSegment(sketch, "E1023", {"start": v(14.09, -15.15) * mm, "end": v(14.46, -15.04) * mm});
            skLineSegment(sketch, "E1024", {"start": v(14.46, -15.04) * mm, "end": v(14.81, -14.85) * mm});
            skLineSegment(sketch, "E1025", {"start": v(14.81, -14.85) * mm, "end": v(15.15, -14.57) * mm});
            skLineSegment(sketch, "E1026", {"start": v(15.15, -14.57) * mm, "end": v(19.15, -10.48) * mm});
            skLineSegment(sketch, "E1027", {"start": v(19.15, -10.48) * mm, "end": v(20, -9.58) * mm});
            skLineSegment(sketch, "E1028", {"start": v(20, -9.58) * mm, "end": v(20.6, -8.95) * mm});
            skLineSegment(sketch, "E1029", {"start": v(20.6, -8.95) * mm, "end": v(21.04, -8.55) * mm});
            skLineSegment(sketch, "E1030", {"start": v(21.04, -8.55) * mm, "end": v(21.45, -8.32) * mm});
            skLineSegment(sketch, "E1031", {"start": v(21.45, -8.32) * mm, "end": v(21.92, -8.22) * mm});
            skLineSegment(sketch, "E1032", {"start": v(21.92, -8.22) * mm, "end": v(22.58, -8.2) * mm});
            skLineSegment(sketch, "E1033", {"start": v(22.58, -8.2) * mm, "end": v(23.52, -8.23) * mm});
            skLineSegment(sketch, "E1034", {"start": v(23.52, -8.23) * mm, "end": v(24.86, -8.23) * mm});
            skLineSegment(sketch, "E1035", {"start": v(24.86, -8.23) * mm, "end": v(26.5, -8.23) * mm});
            skLineSegment(sketch, "E1036", {"start": v(26.5, -8.23) * mm, "end": v(27.71, -8.25) * mm});
            skLineSegment(sketch, "E1037", {"start": v(27.71, -8.25) * mm, "end": v(28.61, -8.25) * mm});
            skLineSegment(sketch, "E1038", {"start": v(28.61, -8.25) * mm, "end": v(29.29, -8.18) * mm});
            skLineSegment(sketch, "E1039", {"start": v(29.29, -8.18) * mm, "end": v(29.82, -8.03) * mm});
            skLineSegment(sketch, "E1040", {"start": v(29.82, -8.03) * mm, "end": v(30.3, -7.75) * mm});
            skLineSegment(sketch, "E1041", {"start": v(30.3, -7.75) * mm, "end": v(30.81, -7.3) * mm});
            skLineSegment(sketch, "E1042", {"start": v(30.81, -7.3) * mm, "end": v(31.46, -6.65) * mm});
            skLineSegment(sketch, "E1043", {"start": v(31.46, -6.65) * mm, "end": v(31.8, -6.24) * mm});
            skLineSegment(sketch, "E1044", {"start": v(31.8, -6.24) * mm, "end": v(31.9, -5.95) * mm});
            skLineSegment(sketch, "E1045", {"start": v(31.9, -5.95) * mm, "end": v(31.79, -5.78) * mm});
            skLineSegment(sketch, "E1046", {"start": v(31.79, -5.78) * mm, "end": v(31.51, -5.7) * mm});
            skLineSegment(sketch, "E1047", {"start": v(31.51, -5.7) * mm, "end": v(31.11, -5.68) * mm});
            skLineSegment(sketch, "E1048", {"start": v(31.11, -5.68) * mm, "end": v(30.63, -5.7) * mm});
            skLineSegment(sketch, "E1049", {"start": v(30.63, -5.7) * mm, "end": v(30.1, -5.73) * mm});
            skLineSegment(sketch, "E1050", {"start": v(30.1, -5.73) * mm, "end": v(29.57, -5.75) * mm});
            skLineSegment(sketch, "E1051", {"start": v(29.57, -5.75) * mm, "end": v(9.56, -5.95) * mm});
            skLineSegment(sketch, "E1052", {"start": v(9.56, -5.95) * mm, "end": v(9.16, -5.95) * mm});
            skLineSegment(sketch, "E1053", {"start": v(9.16, -5.95) * mm, "end": v(8.67, -5.93) * mm});
            skLineSegment(sketch, "E1054", {"start": v(8.67, -5.93) * mm, "end": v(8.12, -5.91) * mm});
            skLineSegment(sketch, "E1055", {"start": v(8.12, -5.91) * mm, "end": v(7.55, -5.9) * mm});
            skLineSegment(sketch, "E1056", {"start": v(7.55, -5.9) * mm, "end": v(7, -5.9) * mm});
            skLineSegment(sketch, "E1057", {"start": v(7, -5.9) * mm, "end": v(6.48, -5.94) * mm});
            skLineSegment(sketch, "E1058", {"start": v(6.48, -5.94) * mm, "end": v(6.06, -6.02) * mm});
            skLineSegment(sketch, "E1059", {"start": v(6.06, -6.02) * mm, "end": v(5.75, -6.13) * mm});
            skLineSegment(sketch, "E1060", {"start": v(5.75, -6.13) * mm, "end": v(5.63, -6.23) * mm});
            skLineSegment(sketch, "E1061", {"start": v(5.63, -6.23) * mm, "end": v(5.4, -6.42) * mm});
            skLineSegment(sketch, "E1062", {"start": v(5.4, -6.42) * mm, "end": v(5.11, -6.7) * mm});
            skLineSegment(sketch, "E1063", {"start": v(5.11, -6.7) * mm, "end": v(4.79, -7.04) * mm});
            skLineSegment(sketch, "E1064", {"start": v(4.79, -7.04) * mm, "end": v(4.47, -7.4) * mm});
            skLineSegment(sketch, "E1065", {"start": v(4.47, -7.4) * mm, "end": v(4.2, -7.76) * mm});
            skLineSegment(sketch, "E1066", {"start": v(4.2, -7.76) * mm, "end": v(4.03, -8.1) * mm});
            skLineSegment(sketch, "E1067", {"start": v(4.03, -8.1) * mm, "end": v(3.98, -8.38) * mm});
            skLineSegment(sketch, "E1068", {"start": v(31.04, 11.33) * mm, "end": v(30.6, 11.4) * mm});
            skLineSegment(sketch, "E1069", {"start": v(30.6, 11.4) * mm, "end": v(30.02, 11.46) * mm});
            skLineSegment(sketch, "E1070", {"start": v(30.02, 11.46) * mm, "end": v(29.36, 11.5) * mm});
            skLineSegment(sketch, "E1071", {"start": v(29.36, 11.5) * mm, "end": v(28.65, 11.51) * mm});
            skLineSegment(sketch, "E1072", {"start": v(28.65, 11.51) * mm, "end": v(27.94, 11.52) * mm});
            skLineSegment(sketch, "E1073", {"start": v(27.94, 11.52) * mm, "end": v(27.25, 11.53) * mm});
            skLineSegment(sketch, "E1074", {"start": v(27.25, 11.53) * mm, "end": v(26.63, 11.54) * mm});
            skLineSegment(sketch, "E1075", {"start": v(26.63, 11.54) * mm, "end": v(26.12, 11.55) * mm});
            skLineSegment(sketch, "E1076", {"start": v(26.12, 11.55) * mm, "end": v(20.43, 11.73) * mm});
            skLineSegment(sketch, "E1077", {"start": v(20.43, 11.73) * mm, "end": v(14.7, 11.87) * mm});
            skLineSegment(sketch, "E1078", {"start": v(14.7, 11.87) * mm, "end": v(8.96, 11.98) * mm});
            skLineSegment(sketch, "E1079", {"start": v(8.96, 11.98) * mm, "end": v(3.2, 12.09) * mm});
            skLineSegment(sketch, "E1080", {"start": v(3.2, 12.09) * mm, "end": v(-2.56, 12.19) * mm});
            skLineSegment(sketch, "E1081", {"start": v(-2.56, 12.19) * mm, "end": v(-8.3, 12.3) * mm});
            skLineSegment(sketch, "E1082", {"start": v(-8.3, 12.3) * mm, "end": v(-14.02, 12.45) * mm});
            skLineSegment(sketch, "E1083", {"start": v(-14.02, 12.45) * mm, "end": v(-19.7, 12.64) * mm});
            skLineSegment(sketch, "E1084", {"start": v(-19.7, 12.64) * mm, "end": v(-20.12, 12.66) * mm});
            skLineSegment(sketch, "E1085", {"start": v(-20.12, 12.66) * mm, "end": v(-20.75, 12.68) * mm});
            skLineSegment(sketch, "E1086", {"start": v(-20.75, 12.68) * mm, "end": v(-21.5, 12.7) * mm});
            skLineSegment(sketch, "E1087", {"start": v(-21.5, 12.7) * mm, "end": v(-22.32, 12.72) * mm});
            skLineSegment(sketch, "E1088", {"start": v(-22.32, 12.72) * mm, "end": v(-23.13, 12.72) * mm});
            skLineSegment(sketch, "E1089", {"start": v(-23.13, 12.72) * mm, "end": v(-23.85, 12.72) * mm});
            skLineSegment(sketch, "E1090", {"start": v(-23.85, 12.72) * mm, "end": v(-24.4, 12.69) * mm});
            skLineSegment(sketch, "E1091", {"start": v(-24.4, 12.69) * mm, "end": v(-24.72, 12.64) * mm});
            skLineSegment(sketch, "E1092", {"start": v(-24.72, 12.64) * mm, "end": v(-36.66, 3.68) * mm});
            skLineSegment(sketch, "E1093", {"start": v(-36.66, 3.68) * mm, "end": v(-38.12, 2.6) * mm});
            skLineSegment(sketch, "E1094", {"start": v(-38.12, 2.6) * mm, "end": v(-38.47, 2.31) * mm});
            skLineSegment(sketch, "E1095", {"start": v(-38.47, 2.31) * mm, "end": v(-38.88, 2) * mm});
            skLineSegment(sketch, "E1096", {"start": v(-38.88, 2) * mm, "end": v(-39.09, 1.84) * mm});
            skLineSegment(sketch, "E1097", {"start": v(-39.09, 1.84) * mm, "end": v(-39.3, 1.72) * mm});
            skLineSegment(sketch, "E1098", {"start": v(-39.3, 1.72) * mm, "end": v(-39.5, 1.63) * mm});
            skLineSegment(sketch, "E1099", {"start": v(-39.5, 1.63) * mm, "end": v(-39.7, 1.58) * mm});
            skLineSegment(sketch, "E1100", {"start": v(-39.7, 1.58) * mm, "end": v(-39.58, 12.98) * mm});
            skLineSegment(sketch, "E1101", {"start": v(-39.58, 12.98) * mm, "end": v(-52.81, 13.21) * mm});
            skLineSegment(sketch, "E1102", {"start": v(-52.81, 13.21) * mm, "end": v(-52.9, 11.9) * mm});
            skLineSegment(sketch, "E1103", {"start": v(-52.9, 11.9) * mm, "end": v(-52.95, 10.22) * mm});
            skLineSegment(sketch, "E1104", {"start": v(-52.95, 10.22) * mm, "end": v(-53, 8.27) * mm});
            skLineSegment(sketch, "E1105", {"start": v(-53, 8.27) * mm, "end": v(-53.03, 6.17) * mm});
            skLineSegment(sketch, "E1106", {"start": v(-53.03, 6.17) * mm, "end": v(-53.05, 4.05) * mm});
            skLineSegment(sketch, "E1107", {"start": v(-53.05, 4.05) * mm, "end": v(-53.07, 2.03) * mm});
            skLineSegment(sketch, "E1108", {"start": v(-53.07, 2.03) * mm, "end": v(-53.08, 0.22) * mm});
            skLineSegment(sketch, "E1109", {"start": v(-53.08, 0.22) * mm, "end": v(-53.1, -1.25) * mm});
            skLineSegment(sketch, "E1110", {"start": v(-53.1, -1.25) * mm, "end": v(-53.12, -1.96) * mm});
            skLineSegment(sketch, "E1111", {"start": v(-53.12, -1.96) * mm, "end": v(-53.15, -2.47) * mm});
            skLineSegment(sketch, "E1112", {"start": v(-53.15, -2.47) * mm, "end": v(-53.14, -2.82) * mm});
            skLineSegment(sketch, "E1113", {"start": v(-53.14, -2.82) * mm, "end": v(-53.06, -3.04) * mm});
            skLineSegment(sketch, "E1114", {"start": v(-53.06, -3.04) * mm, "end": v(-52.89, -3.16) * mm});
            skLineSegment(sketch, "E1115", {"start": v(-52.89, -3.16) * mm, "end": v(-52.58, -3.2) * mm});
            skLineSegment(sketch, "E1116", {"start": v(-52.58, -3.2) * mm, "end": v(-52.1, -3.22) * mm});
            skLineSegment(sketch, "E1117", {"start": v(-52.1, -3.22) * mm, "end": v(-51.42, -3.22) * mm});
            skLineSegment(sketch, "E1118", {"start": v(-51.42, -3.22) * mm, "end": v(-47.77, -3.24) * mm});
            skLineSegment(sketch, "E1119", {"start": v(-47.77, -3.24) * mm, "end": v(-40.52, -3.35) * mm});
            skLineSegment(sketch, "E1120", {"start": v(-40.52, -3.35) * mm, "end": v(2.78, -4.19) * mm});
            skLineSegment(sketch, "E1121", {"start": v(2.78, -4.19) * mm, "end": v(3.38, -4.2) * mm});
            skLineSegment(sketch, "E1122", {"start": v(3.38, -4.2) * mm, "end": v(4.28, -4.23) * mm});
            skLineSegment(sketch, "E1123", {"start": v(4.28, -4.23) * mm, "end": v(5.36, -4.26) * mm});
            skLineSegment(sketch, "E1124", {"start": v(5.36, -4.26) * mm, "end": v(6.52, -4.3) * mm});
            skLineSegment(sketch, "E1125", {"start": v(6.52, -4.3) * mm, "end": v(7.66, -4.3) * mm});
            skLineSegment(sketch, "E1126", {"start": v(7.66, -4.3) * mm, "end": v(8.67, -4.3) * mm});
            skLineSegment(sketch, "E1127", {"start": v(8.67, -4.3) * mm, "end": v(9.44, -4.27) * mm});
            skLineSegment(sketch, "E1128", {"start": v(9.44, -4.27) * mm, "end": v(9.86, -4.2) * mm});
            skLineSegment(sketch, "E1129", {"start": v(9.86, -4.2) * mm, "end": v(22.66, 5.12) * mm});
            skLineSegment(sketch, "E1130", {"start": v(22.66, 5.12) * mm, "end": v(23.24, 5.53) * mm});
            skLineSegment(sketch, "E1131", {"start": v(23.24, 5.53) * mm, "end": v(24.24, 6.25) * mm});
            skLineSegment(sketch, "E1132", {"start": v(24.24, 6.25) * mm, "end": v(25.53, 7.18) * mm});
            skLineSegment(sketch, "E1133", {"start": v(25.53, 7.18) * mm, "end": v(26.96, 8.21) * mm});
            skLineSegment(sketch, "E1134", {"start": v(26.96, 8.21) * mm, "end": v(28.37, 9.24) * mm});
            skLineSegment(sketch, "E1135", {"start": v(28.37, 9.24) * mm, "end": v(29.62, 10.18) * mm});
            skLineSegment(sketch, "E1136", {"start": v(29.62, 10.18) * mm, "end": v(30.56, 10.9) * mm});
            skLineSegment(sketch, "E1137", {"start": v(30.56, 10.9) * mm, "end": v(31.04, 11.33) * mm});
            skLineSegment(sketch, "E1138", {"start": v(-7.16, 4.87) * mm, "end": v(-6.07, 4.8) * mm});
            skLineSegment(sketch, "E1139", {"start": v(-6.07, 4.8) * mm, "end": v(-4.96, 4.75) * mm});
            skLineSegment(sketch, "E1140", {"start": v(-4.96, 4.75) * mm, "end": v(-3.83, 4.72) * mm});
            skLineSegment(sketch, "E1141", {"start": v(-3.83, 4.72) * mm, "end": v(-2.69, 4.7) * mm});
            skLineSegment(sketch, "E1142", {"start": v(-2.69, 4.7) * mm, "end": v(-1.55, 4.68) * mm});
            skLineSegment(sketch, "E1143", {"start": v(-1.55, 4.68) * mm, "end": v(-0.41, 4.67) * mm});
            skLineSegment(sketch, "E1144", {"start": v(-0.41, 4.67) * mm, "end": v(0.71, 4.66) * mm});
            skLineSegment(sketch, "E1145", {"start": v(0.71, 4.66) * mm, "end": v(1.81, 4.64) * mm});
            skLineSegment(sketch, "E1146", {"start": v(1.81, 4.64) * mm, "end": v(15.3, 4.33) * mm});
            skLineSegment(sketch, "E1147", {"start": v(15.3, 4.33) * mm, "end": v(15.83, 4.32) * mm});
            skLineSegment(sketch, "E1148", {"start": v(15.83, 4.32) * mm, "end": v(16.24, 4.36) * mm});
            skLineSegment(sketch, "E1149", {"start": v(16.24, 4.36) * mm, "end": v(16.58, 4.45) * mm});
            skLineSegment(sketch, "E1150", {"start": v(16.58, 4.45) * mm, "end": v(16.88, 4.59) * mm});
            skLineSegment(sketch, "E1151", {"start": v(16.88, 4.59) * mm, "end": v(17.18, 4.78) * mm});
            skLineSegment(sketch, "E1152", {"start": v(17.18, 4.78) * mm, "end": v(17.52, 5.04) * mm});
            skLineSegment(sketch, "E1153", {"start": v(17.52, 5.04) * mm, "end": v(17.94, 5.37) * mm});
            skLineSegment(sketch, "E1154", {"start": v(17.94, 5.37) * mm, "end": v(18.48, 5.78) * mm});
            skLineSegment(sketch, "E1155", {"start": v(18.48, 5.78) * mm, "end": v(19.16, 6.27) * mm});
            skLineSegment(sketch, "E1156", {"start": v(19.16, 6.27) * mm, "end": v(19.82, 6.73) * mm});
            skLineSegment(sketch, "E1157", {"start": v(19.82, 6.73) * mm, "end": v(20.48, 7.2) * mm});
            skLineSegment(sketch, "E1158", {"start": v(20.48, 7.2) * mm, "end": v(21.16, 7.72) * mm});
            skLineSegment(sketch, "E1159", {"start": v(21.16, 7.72) * mm, "end": v(21.73, 8.14) * mm});
            skLineSegment(sketch, "E1160", {"start": v(21.73, 8.14) * mm, "end": v(22.54, 8.71) * mm});
            skLineSegment(sketch, "E1161", {"start": v(22.54, 8.71) * mm, "end": v(22.94, 9.01) * mm});
            skLineSegment(sketch, "E1162", {"start": v(22.94, 9.01) * mm, "end": v(23.29, 9.3) * mm});
            skLineSegment(sketch, "E1163", {"start": v(23.29, 9.3) * mm, "end": v(23.55, 9.56) * mm});
            skLineSegment(sketch, "E1164", {"start": v(23.55, 9.56) * mm, "end": v(23.7, 9.77) * mm});
            skLineSegment(sketch, "E1165", {"start": v(23.7, 9.77) * mm, "end": v(21.48, 9.8) * mm});
            skLineSegment(sketch, "E1166", {"start": v(21.48, 9.8) * mm, "end": v(19.24, 9.84) * mm});
            skLineSegment(sketch, "E1167", {"start": v(19.24, 9.84) * mm, "end": v(17, 9.9) * mm});
            skLineSegment(sketch, "E1168", {"start": v(17, 9.9) * mm, "end": v(14.76, 9.96) * mm});
            skLineSegment(sketch, "E1169", {"start": v(14.76, 9.96) * mm, "end": v(12.51, 10.03) * mm});
            skLineSegment(sketch, "E1170", {"start": v(12.51, 10.03) * mm, "end": v(10.27, 10.1) * mm});
            skLineSegment(sketch, "E1171", {"start": v(10.27, 10.1) * mm, "end": v(8.03, 10.17) * mm});
            skLineSegment(sketch, "E1172", {"start": v(8.03, 10.17) * mm, "end": v(5.8, 10.23) * mm});
            skLineSegment(sketch, "E1173", {"start": v(5.8, 10.23) * mm, "end": v(1.2, 10.34) * mm});
            skLineSegment(sketch, "E1174", {"start": v(1.2, 10.34) * mm, "end": v(0.7, 10.35) * mm});
            skLineSegment(sketch, "E1175", {"start": v(0.7, 10.35) * mm, "end": v(0.3, 10.3) * mm});
            skLineSegment(sketch, "E1176", {"start": v(0.3, 10.3) * mm, "end": v(-0.05, 10.22) * mm});
            skLineSegment(sketch, "E1177", {"start": v(-0.05, 10.22) * mm, "end": v(-0.37, 10.08) * mm});
            skLineSegment(sketch, "E1178", {"start": v(-0.37, 10.08) * mm, "end": v(-0.7, 9.88) * mm});
            skLineSegment(sketch, "E1179", {"start": v(-0.7, 9.88) * mm, "end": v(-1.05, 9.62) * mm});
            skLineSegment(sketch, "E1180", {"start": v(-1.05, 9.62) * mm, "end": v(-1.48, 9.29) * mm});
            skLineSegment(sketch, "E1181", {"start": v(-1.48, 9.29) * mm, "end": v(-2, 8.88) * mm});
            skLineSegment(sketch, "E1182", {"start": v(-2, 8.88) * mm, "end": v(-2.35, 8.62) * mm});
            skLineSegment(sketch, "E1183", {"start": v(-2.35, 8.62) * mm, "end": v(-2.98, 8.16) * mm});
            skLineSegment(sketch, "E1184", {"start": v(-2.98, 8.16) * mm, "end": v(-3.8, 7.57) * mm});
            skLineSegment(sketch, "E1185", {"start": v(-3.8, 7.57) * mm, "end": v(-4.7, 6.92) * mm});
            skLineSegment(sketch, "E1186", {"start": v(-4.7, 6.92) * mm, "end": v(-5.58, 6.26) * mm});
            skLineSegment(sketch, "E1187", {"start": v(-5.58, 6.26) * mm, "end": v(-6.35, 5.65) * mm});
            skLineSegment(sketch, "E1188", {"start": v(-6.35, 5.65) * mm, "end": v(-6.9, 5.17) * mm});
            skLineSegment(sketch, "E1189", {"start": v(-6.9, 5.17) * mm, "end": v(-7.16, 4.87) * mm});
            skLineSegment(sketch, "E1190", {"start": v(-34.93, -1.65) * mm, "end": v(-33.66, -1.74) * mm});
            skLineSegment(sketch, "E1191", {"start": v(-33.66, -1.74) * mm, "end": v(-32, -1.8) * mm});
            skLineSegment(sketch, "E1192", {"start": v(-32, -1.8) * mm, "end": v(-30.08, -1.84) * mm});
            skLineSegment(sketch, "E1193", {"start": v(-30.08, -1.84) * mm, "end": v(-28, -1.87) * mm});
            skLineSegment(sketch, "E1194", {"start": v(-28, -1.87) * mm, "end": v(-25.86, -1.89) * mm});
            skLineSegment(sketch, "E1195", {"start": v(-25.86, -1.89) * mm, "end": v(-23.82, -1.9) * mm});
            skLineSegment(sketch, "E1196", {"start": v(-23.82, -1.9) * mm, "end": v(-21.96, -1.93) * mm});
            skLineSegment(sketch, "E1197", {"start": v(-21.96, -1.93) * mm, "end": v(-20.43, -1.96) * mm});
            skLineSegment(sketch, "E1198", {"start": v(-20.43, -1.96) * mm, "end": v(-19.78, -1.97) * mm});
            skLineSegment(sketch, "E1199", {"start": v(-19.78, -1.97) * mm, "end": v(-19.29, -1.92) * mm});
            skLineSegment(sketch, "E1200", {"start": v(-19.29, -1.92) * mm, "end": v(-18.9, -1.82) * mm});
            skLineSegment(sketch, "E1201", {"start": v(-18.9, -1.82) * mm, "end": v(-18.53, -1.65) * mm});
            skLineSegment(sketch, "E1202", {"start": v(-18.53, -1.65) * mm, "end": v(-18.16, -1.39) * mm});
            skLineSegment(sketch, "E1203", {"start": v(-18.16, -1.39) * mm, "end": v(-17.7, -1.03) * mm});
            skLineSegment(sketch, "E1204", {"start": v(-17.7, -1.03) * mm, "end": v(-17.13, -0.56) * mm});
            skLineSegment(sketch, "E1205", {"start": v(-17.13, -0.56) * mm, "end": v(-16.36, 0.03) * mm});
            skLineSegment(sketch, "E1206", {"start": v(-16.36, 0.03) * mm, "end": v(-15.96, 0.3) * mm});
            skLineSegment(sketch, "E1207", {"start": v(-15.96, 0.3) * mm, "end": v(-15.48, 0.65) * mm});
            skLineSegment(sketch, "E1208", {"start": v(-15.48, 0.65) * mm, "end": v(-15.25, 0.83) * mm});
            skLineSegment(sketch, "E1209", {"start": v(-15.25, 0.83) * mm, "end": v(-15.03, 1.02) * mm});
            skLineSegment(sketch, "E1210", {"start": v(-15.03, 1.02) * mm, "end": v(-14.86, 1.2) * mm});
            skLineSegment(sketch, "E1211", {"start": v(-14.86, 1.2) * mm, "end": v(-14.74, 1.38) * mm});
            skLineSegment(sketch, "E1212", {"start": v(-14.74, 1.38) * mm, "end": v(-16.17, 1.46) * mm});
            skLineSegment(sketch, "E1213", {"start": v(-16.17, 1.46) * mm, "end": v(-17.62, 1.53) * mm});
            skLineSegment(sketch, "E1214", {"start": v(-17.62, 1.53) * mm, "end": v(-19.08, 1.57) * mm});
            skLineSegment(sketch, "E1215", {"start": v(-19.08, 1.57) * mm, "end": v(-20.55, 1.6) * mm});
            skLineSegment(sketch, "E1216", {"start": v(-20.55, 1.6) * mm, "end": v(-22.02, 1.61) * mm});
            skLineSegment(sketch, "E1217", {"start": v(-22.02, 1.61) * mm, "end": v(-23.49, 1.62) * mm});
            skLineSegment(sketch, "E1218", {"start": v(-23.49, 1.62) * mm, "end": v(-24.94, 1.64) * mm});
            skLineSegment(sketch, "E1219", {"start": v(-24.94, 1.64) * mm, "end": v(-26.38, 1.66) * mm});
            skLineSegment(sketch, "E1220", {"start": v(-26.38, 1.66) * mm, "end": v(-29.3, 1.7) * mm});
            skLineSegment(sketch, "E1221", {"start": v(-29.3, 1.7) * mm, "end": v(-29.81, 1.7) * mm});
            skLineSegment(sketch, "E1222", {"start": v(-29.81, 1.7) * mm, "end": v(-30.2, 1.7) * mm});
            skLineSegment(sketch, "E1223", {"start": v(-30.2, 1.7) * mm, "end": v(-30.47, 1.67) * mm});
            skLineSegment(sketch, "E1224", {"start": v(-30.47, 1.67) * mm, "end": v(-30.7, 1.62) * mm});
            skLineSegment(sketch, "E1225", {"start": v(-30.7, 1.62) * mm, "end": v(-30.88, 1.54) * mm});
            skLineSegment(sketch, "E1226", {"start": v(-30.88, 1.54) * mm, "end": v(-31.09, 1.4) * mm});
            skLineSegment(sketch, "E1227", {"start": v(-31.09, 1.4) * mm, "end": v(-31.33, 1.23) * mm});
            skLineSegment(sketch, "E1228", {"start": v(-31.33, 1.23) * mm, "end": v(-31.66, 0.99) * mm});
            skLineSegment(sketch, "E1229", {"start": v(-31.66, 0.99) * mm, "end": v(-31.93, 0.79) * mm});
            skLineSegment(sketch, "E1230", {"start": v(-31.93, 0.79) * mm, "end": v(-32.36, 0.48) * mm});
            skLineSegment(sketch, "E1231", {"start": v(-32.36, 0.48) * mm, "end": v(-32.88, 0.1) * mm});
            skLineSegment(sketch, "E1232", {"start": v(-32.88, 0.1) * mm, "end": v(-33.45, -0.33) * mm});
            skLineSegment(sketch, "E1233", {"start": v(-33.45, -0.33) * mm, "end": v(-33.99, -0.75) * mm});
            skLineSegment(sketch, "E1234", {"start": v(-33.99, -0.75) * mm, "end": v(-34.46, -1.14) * mm});
            skLineSegment(sketch, "E1235", {"start": v(-34.46, -1.14) * mm, "end": v(-34.79, -1.45) * mm});
            skLineSegment(sketch, "E1236", {"start": v(-34.79, -1.45) * mm, "end": v(-34.93, -1.65) * mm});
            skLineSegment(sketch, "E1237", {"start": v(-28.66, 3) * mm, "end": v(-27.84, 2.9) * mm});
            skLineSegment(sketch, "E1238", {"start": v(-27.84, 2.9) * mm, "end": v(-26.33, 2.82) * mm});
            skLineSegment(sketch, "E1239", {"start": v(-26.33, 2.82) * mm, "end": v(-24.35, 2.76) * mm});
            skLineSegment(sketch, "E1240", {"start": v(-24.35, 2.76) * mm, "end": v(-22.08, 2.72) * mm});
            skLineSegment(sketch, "E1241", {"start": v(-22.08, 2.72) * mm, "end": v(-19.74, 2.7) * mm});
            skLineSegment(sketch, "E1242", {"start": v(-19.74, 2.7) * mm, "end": v(-17.51, 2.67) * mm});
            skLineSegment(sketch, "E1243", {"start": v(-17.51, 2.67) * mm, "end": v(-15.6, 2.65) * mm});
            skLineSegment(sketch, "E1244", {"start": v(-15.6, 2.65) * mm, "end": v(-14.23, 2.63) * mm});
            skLineSegment(sketch, "E1245", {"start": v(-14.23, 2.63) * mm, "end": v(-13.6, 2.63) * mm});
            skLineSegment(sketch, "E1246", {"start": v(-13.6, 2.63) * mm, "end": v(-13.1, 2.7) * mm});
            skLineSegment(sketch, "E1247", {"start": v(-13.1, 2.7) * mm, "end": v(-12.67, 2.81) * mm});
            skLineSegment(sketch, "E1248", {"start": v(-12.67, 2.81) * mm, "end": v(-12.3, 3) * mm});
            skLineSegment(sketch, "E1249", {"start": v(-12.3, 3) * mm, "end": v(-11.9, 3.27) * mm});
            skLineSegment(sketch, "E1250", {"start": v(-11.9, 3.27) * mm, "end": v(-11.46, 3.61) * mm});
            skLineSegment(sketch, "E1251", {"start": v(-11.46, 3.61) * mm, "end": v(-10.91, 4.05) * mm});
            skLineSegment(sketch, "E1252", {"start": v(-10.91, 4.05) * mm, "end": v(-10.22, 4.58) * mm});
            skLineSegment(sketch, "E1253", {"start": v(-10.22, 4.58) * mm, "end": v(-9.78, 4.9) * mm});
            skLineSegment(sketch, "E1254", {"start": v(-9.78, 4.9) * mm, "end": v(-9.36, 5.2) * mm});
            skLineSegment(sketch, "E1255", {"start": v(-9.36, 5.2) * mm, "end": v(-9.15, 5.36) * mm});
            skLineSegment(sketch, "E1256", {"start": v(-9.15, 5.36) * mm, "end": v(-8.95, 5.52) * mm});
            skLineSegment(sketch, "E1257", {"start": v(-8.95, 5.52) * mm, "end": v(-8.76, 5.7) * mm});
            skLineSegment(sketch, "E1258", {"start": v(-8.76, 5.7) * mm, "end": v(-8.58, 5.87) * mm});
            skLineSegment(sketch, "E1259", {"start": v(-8.58, 5.87) * mm, "end": v(-9.4, 5.98) * mm});
            skLineSegment(sketch, "E1260", {"start": v(-9.4, 5.98) * mm, "end": v(-11.04, 6.07) * mm});
            skLineSegment(sketch, "E1261", {"start": v(-11.04, 6.07) * mm, "end": v(-13.23, 6.13) * mm});
            skLineSegment(sketch, "E1262", {"start": v(-13.23, 6.13) * mm, "end": v(-15.72, 6.18) * mm});
            skLineSegment(sketch, "E1263", {"start": v(-15.72, 6.18) * mm, "end": v(-18.25, 6.22) * mm});
            skLineSegment(sketch, "E1264", {"start": v(-18.25, 6.22) * mm, "end": v(-20.58, 6.24) * mm});
            skLineSegment(sketch, "E1265", {"start": v(-20.58, 6.24) * mm, "end": v(-22.44, 6.25) * mm});
            skLineSegment(sketch, "E1266", {"start": v(-22.44, 6.25) * mm, "end": v(-23.59, 6.25) * mm});
            skLineSegment(sketch, "E1267", {"start": v(-23.59, 6.25) * mm, "end": v(-23.93, 6.25) * mm});
            skLineSegment(sketch, "E1268", {"start": v(-23.93, 6.25) * mm, "end": v(-24.2, 6.24) * mm});
            skLineSegment(sketch, "E1269", {"start": v(-24.2, 6.24) * mm, "end": v(-24.4, 6.22) * mm});
            skLineSegment(sketch, "E1270", {"start": v(-24.4, 6.22) * mm, "end": v(-24.56, 6.19) * mm});
            skLineSegment(sketch, "E1271", {"start": v(-24.56, 6.19) * mm, "end": v(-24.7, 6.13) * mm});
            skLineSegment(sketch, "E1272", {"start": v(-24.7, 6.13) * mm, "end": v(-24.86, 6.04) * mm});
            skLineSegment(sketch, "E1273", {"start": v(-24.86, 6.04) * mm, "end": v(-25.03, 5.92) * mm});
            skLineSegment(sketch, "E1274", {"start": v(-25.03, 5.92) * mm, "end": v(-25.25, 5.76) * mm});
            skLineSegment(sketch, "E1275", {"start": v(-25.25, 5.76) * mm, "end": v(-25.6, 5.5) * mm});
            skLineSegment(sketch, "E1276", {"start": v(-25.6, 5.5) * mm, "end": v(-26.06, 5.17) * mm});
            skLineSegment(sketch, "E1277", {"start": v(-26.06, 5.17) * mm, "end": v(-26.58, 4.8) * mm});
            skLineSegment(sketch, "E1278", {"start": v(-26.58, 4.8) * mm, "end": v(-27.11, 4.4) * mm});
            skLineSegment(sketch, "E1279", {"start": v(-27.11, 4.4) * mm, "end": v(-27.63, 4) * mm});
            skLineSegment(sketch, "E1280", {"start": v(-27.63, 4) * mm, "end": v(-28.09, 3.63) * mm});
            skLineSegment(sketch, "E1281", {"start": v(-28.09, 3.63) * mm, "end": v(-28.44, 3.29) * mm});
            skLineSegment(sketch, "E1282", {"start": v(-28.44, 3.29) * mm, "end": v(-28.66, 3) * mm});
            skLineSegment(sketch, "E1283", {"start": v(-16.45, -1.83) * mm, "end": v(-16.2, -1.95) * mm});
            skLineSegment(sketch, "E1284", {"start": v(-16.2, -1.95) * mm, "end": v(-15.84, -2.03) * mm});
            skLineSegment(sketch, "E1285", {"start": v(-15.84, -2.03) * mm, "end": v(-15.39, -2.08) * mm});
            skLineSegment(sketch, "E1286", {"start": v(-15.39, -2.08) * mm, "end": v(-14.88, -2.1) * mm});
            skLineSegment(sketch, "E1287", {"start": v(-14.88, -2.1) * mm, "end": v(-14.36, -2.1) * mm});
            skLineSegment(sketch, "E1288", {"start": v(-14.36, -2.1) * mm, "end": v(-13.85, -2.1) * mm});
            skLineSegment(sketch, "E1289", {"start": v(-13.85, -2.1) * mm, "end": v(-13.39, -2.1) * mm});
            skLineSegment(sketch, "E1290", {"start": v(-13.39, -2.1) * mm, "end": v(-13.01, -2.1) * mm});
            skLineSegment(sketch, "E1291", {"start": v(-13.01, -2.1) * mm, "end": v(-9.38, -2.17) * mm});
            skLineSegment(sketch, "E1292", {"start": v(-9.38, -2.17) * mm, "end": v(4.97, -2.46) * mm});
            skLineSegment(sketch, "E1293", {"start": v(4.97, -2.46) * mm, "end": v(5.41, -2.48) * mm});
            skLineSegment(sketch, "E1294", {"start": v(5.41, -2.48) * mm, "end": v(5.9, -2.5) * mm});
            skLineSegment(sketch, "E1295", {"start": v(5.9, -2.5) * mm, "end": v(6.37, -2.52) * mm});
            skLineSegment(sketch, "E1296", {"start": v(6.37, -2.52) * mm, "end": v(6.8, -2.51) * mm});
            skLineSegment(sketch, "E1297", {"start": v(6.8, -2.51) * mm, "end": v(7.19, -2.4) * mm});
            skLineSegment(sketch, "E1298", {"start": v(7.19, -2.4) * mm, "end": v(7.67, -2.15) * mm});
            skLineSegment(sketch, "E1299", {"start": v(7.67, -2.15) * mm, "end": v(8.2, -1.79) * mm});
            skLineSegment(sketch, "E1300", {"start": v(8.2, -1.79) * mm, "end": v(8.74, -1.38) * mm});
            skLineSegment(sketch, "E1301", {"start": v(8.74, -1.38) * mm, "end": v(9.24, -0.97) * mm});
            skLineSegment(sketch, "E1302", {"start": v(9.24, -0.97) * mm, "end": v(9.66, -0.6) * mm});
            skLineSegment(sketch, "E1303", {"start": v(9.66, -0.6) * mm, "end": v(9.95, -0.33) * mm});
            skLineSegment(sketch, "E1304", {"start": v(9.95, -0.33) * mm, "end": v(10.07, -0.2) * mm});
            skLineSegment(sketch, "E1305", {"start": v(10.07, -0.2) * mm, "end": v(-12.53, 0.3) * mm});
            skLineSegment(sketch, "E1306", {"start": v(-12.53, 0.3) * mm, "end": v(-13.16, 0.25) * mm});
            skLineSegment(sketch, "E1307", {"start": v(-13.16, 0.25) * mm, "end": v(-13.69, 0.11) * mm});
            skLineSegment(sketch, "E1308", {"start": v(-13.69, 0.11) * mm, "end": v(-14.15, -0.1) * mm});
            skLineSegment(sketch, "E1309", {"start": v(-14.15, -0.1) * mm, "end": v(-14.58, -0.4) * mm});
            skLineSegment(sketch, "E1310", {"start": v(-14.58, -0.4) * mm, "end": v(-15, -0.72) * mm});
            skLineSegment(sketch, "E1311", {"start": v(-15, -0.72) * mm, "end": v(-15.42, -1.08) * mm});
            skLineSegment(sketch, "E1312", {"start": v(-15.42, -1.08) * mm, "end": v(-15.9, -1.46) * mm});
            skLineSegment(sketch, "E1313", {"start": v(-15.9, -1.46) * mm, "end": v(-16.45, -1.83) * mm});
            skLineSegment(sketch, "E1314", {"start": v(-22.58, 7.55) * mm, "end": v(-21.17, 7.47) * mm});
            skLineSegment(sketch, "E1315", {"start": v(-21.17, 7.47) * mm, "end": v(-19.75, 7.4) * mm});
            skLineSegment(sketch, "E1316", {"start": v(-19.75, 7.4) * mm, "end": v(-18.32, 7.37) * mm});
            skLineSegment(sketch, "E1317", {"start": v(-18.32, 7.37) * mm, "end": v(-16.9, 7.34) * mm});
            skLineSegment(sketch, "E1318", {"start": v(-16.9, 7.34) * mm, "end": v(-15.46, 7.32) * mm});
            skLineSegment(sketch, "E1319", {"start": v(-15.46, 7.32) * mm, "end": v(-14.03, 7.3) * mm});
            skLineSegment(sketch, "E1320", {"start": v(-14.03, 7.3) * mm, "end": v(-12.61, 7.28) * mm});
            skLineSegment(sketch, "E1321", {"start": v(-12.61, 7.28) * mm, "end": v(-11.2, 7.25) * mm});
            skLineSegment(sketch, "E1322", {"start": v(-11.2, 7.25) * mm, "end": v(-8.28, 7.21) * mm});
            skLineSegment(sketch, "E1323", {"start": v(-8.28, 7.21) * mm, "end": v(-7.76, 7.2) * mm});
            skLineSegment(sketch, "E1324", {"start": v(-7.76, 7.2) * mm, "end": v(-7.38, 7.18) * mm});
            skLineSegment(sketch, "E1325", {"start": v(-7.38, 7.18) * mm, "end": v(-7.1, 7.17) * mm});
            skLineSegment(sketch, "E1326", {"start": v(-7.1, 7.17) * mm, "end": v(-6.89, 7.2) * mm});
            skLineSegment(sketch, "E1327", {"start": v(-6.89, 7.2) * mm, "end": v(-6.7, 7.26) * mm});
            skLineSegment(sketch, "E1328", {"start": v(-6.7, 7.26) * mm, "end": v(-6.49, 7.36) * mm});
            skLineSegment(sketch, "E1329", {"start": v(-6.49, 7.36) * mm, "end": v(-6.23, 7.54) * mm});
            skLineSegment(sketch, "E1330", {"start": v(-6.23, 7.54) * mm, "end": v(-5.88, 7.78) * mm});
            skLineSegment(sketch, "E1331", {"start": v(-5.88, 7.78) * mm, "end": v(-5.61, 7.97) * mm});
            skLineSegment(sketch, "E1332", {"start": v(-5.61, 7.97) * mm, "end": v(-5.19, 8.28) * mm});
            skLineSegment(sketch, "E1333", {"start": v(-5.19, 8.28) * mm, "end": v(-4.67, 8.66) * mm});
            skLineSegment(sketch, "E1334", {"start": v(-4.67, 8.66) * mm, "end": v(-4.1, 9.07) * mm});
            skLineSegment(sketch, "E1335", {"start": v(-4.1, 9.07) * mm, "end": v(-3.57, 9.49) * mm});
            skLineSegment(sketch, "E1336", {"start": v(-3.57, 9.49) * mm, "end": v(-3.1, 9.86) * mm});
            skLineSegment(sketch, "E1337", {"start": v(-3.1, 9.86) * mm, "end": v(-2.78, 10.16) * mm});
            skLineSegment(sketch, "E1338", {"start": v(-2.78, 10.16) * mm, "end": v(-2.65, 10.33) * mm});
            skLineSegment(sketch, "E1339", {"start": v(-2.65, 10.33) * mm, "end": v(-3.44, 10.41) * mm});
            skLineSegment(sketch, "E1340", {"start": v(-3.44, 10.41) * mm, "end": v(-4.71, 10.47) * mm});
            skLineSegment(sketch, "E1341", {"start": v(-4.71, 10.47) * mm, "end": v(-6.33, 10.53) * mm});
            skLineSegment(sketch, "E1342", {"start": v(-6.33, 10.53) * mm, "end": v(-8.12, 10.57) * mm});
            skLineSegment(sketch, "E1343", {"start": v(-8.12, 10.57) * mm, "end": v(-9.95, 10.6) * mm});
            skLineSegment(sketch, "E1344", {"start": v(-9.95, 10.6) * mm, "end": v(-11.66, 10.63) * mm});
            skLineSegment(sketch, "E1345", {"start": v(-11.66, 10.63) * mm, "end": v(-13.1, 10.65) * mm});
            skLineSegment(sketch, "E1346", {"start": v(-13.1, 10.65) * mm, "end": v(-14.1, 10.66) * mm});
            skLineSegment(sketch, "E1347", {"start": v(-14.1, 10.66) * mm, "end": v(-16.9, 10.73) * mm});
            skLineSegment(sketch, "E1348", {"start": v(-16.9, 10.73) * mm, "end": v(-17.39, 10.75) * mm});
            skLineSegment(sketch, "E1349", {"start": v(-17.39, 10.75) * mm, "end": v(-17.76, 10.76) * mm});
            skLineSegment(sketch, "E1350", {"start": v(-17.76, 10.76) * mm, "end": v(-18.06, 10.75) * mm});
            skLineSegment(sketch, "E1351", {"start": v(-18.06, 10.75) * mm, "end": v(-18.3, 10.72) * mm});
            skLineSegment(sketch, "E1352", {"start": v(-18.3, 10.72) * mm, "end": v(-18.52, 10.65) * mm});
            skLineSegment(sketch, "E1353", {"start": v(-18.52, 10.65) * mm, "end": v(-18.74, 10.54) * mm});
            skLineSegment(sketch, "E1354", {"start": v(-18.74, 10.54) * mm, "end": v(-19, 10.38) * mm});
            skLineSegment(sketch, "E1355", {"start": v(-19, 10.38) * mm, "end": v(-19.31, 10.15) * mm});
            skLineSegment(sketch, "E1356", {"start": v(-19.31, 10.15) * mm, "end": v(-19.61, 9.94) * mm});
            skLineSegment(sketch, "E1357", {"start": v(-19.61, 9.94) * mm, "end": v(-20.05, 9.63) * mm});
            skLineSegment(sketch, "E1358", {"start": v(-20.05, 9.63) * mm, "end": v(-20.56, 9.26) * mm});
            skLineSegment(sketch, "E1359", {"start": v(-20.56, 9.26) * mm, "end": v(-21.1, 8.86) * mm});
            skLineSegment(sketch, "E1360", {"start": v(-21.1, 8.86) * mm, "end": v(-21.62, 8.46) * mm});
            skLineSegment(sketch, "E1361", {"start": v(-21.62, 8.46) * mm, "end": v(-22.07, 8.09) * mm});
            skLineSegment(sketch, "E1362", {"start": v(-22.07, 8.09) * mm, "end": v(-22.4, 7.77) * mm});
            skLineSegment(sketch, "E1363", {"start": v(-22.4, 7.77) * mm, "end": v(-22.58, 7.55) * mm});
            skLineSegment(sketch, "E1364", {"start": v(-11.53, 1.6) * mm, "end": v(-8.74, 1.52) * mm});
            skLineSegment(sketch, "E1365", {"start": v(-8.74, 1.52) * mm, "end": v(-5.89, 1.44) * mm});
            skLineSegment(sketch, "E1366", {"start": v(-5.89, 1.44) * mm, "end": v(-3, 1.36) * mm});
            skLineSegment(sketch, "E1367", {"start": v(-3, 1.36) * mm, "end": v(-0.08, 1.28) * mm});
            skLineSegment(sketch, "E1368", {"start": v(-0.08, 1.28) * mm, "end": v(2.82, 1.21) * mm});
            skLineSegment(sketch, "E1369", {"start": v(2.82, 1.21) * mm, "end": v(5.7, 1.15) * mm});
            skLineSegment(sketch, "E1370", {"start": v(5.7, 1.15) * mm, "end": v(8.53, 1.11) * mm});
            skLineSegment(sketch, "E1371", {"start": v(8.53, 1.11) * mm, "end": v(11.29, 1.1) * mm});
            skLineSegment(sketch, "E1372", {"start": v(11.29, 1.1) * mm, "end": v(11.8, 1.16) * mm});
            skLineSegment(sketch, "E1373", {"start": v(11.8, 1.16) * mm, "end": v(12.34, 1.36) * mm});
            skLineSegment(sketch, "E1374", {"start": v(12.34, 1.36) * mm, "end": v(12.88, 1.64) * mm});
            skLineSegment(sketch, "E1375", {"start": v(12.88, 1.64) * mm, "end": v(13.38, 1.97) * mm});
            skLineSegment(sketch, "E1376", {"start": v(13.38, 1.97) * mm, "end": v(13.83, 2.32) * mm});
            skLineSegment(sketch, "E1377", {"start": v(13.83, 2.32) * mm, "end": v(14.2, 2.65) * mm});
            skLineSegment(sketch, "E1378", {"start": v(14.2, 2.65) * mm, "end": v(14.47, 2.92) * mm});
            skLineSegment(sketch, "E1379", {"start": v(14.47, 2.92) * mm, "end": v(14.6, 3.1) * mm});
            skLineSegment(sketch, "E1380", {"start": v(14.6, 3.1) * mm, "end": v(11.95, 3.22) * mm});
            skLineSegment(sketch, "E1381", {"start": v(11.95, 3.22) * mm, "end": v(9.16, 3.31) * mm});
            skLineSegment(sketch, "E1382", {"start": v(9.16, 3.31) * mm, "end": v(6.28, 3.39) * mm});
            skLineSegment(sketch, "E1383", {"start": v(6.28, 3.39) * mm, "end": v(3.34, 3.44) * mm});
            skLineSegment(sketch, "E1384", {"start": v(3.34, 3.44) * mm, "end": v(0.4, 3.49) * mm});
            skLineSegment(sketch, "E1385", {"start": v(0.4, 3.49) * mm, "end": v(-2.54, 3.53) * mm});
            skLineSegment(sketch, "E1386", {"start": v(-2.54, 3.53) * mm, "end": v(-5.4, 3.57) * mm});
            skLineSegment(sketch, "E1387", {"start": v(-5.4, 3.57) * mm, "end": v(-8.16, 3.61) * mm});
            skLineSegment(sketch, "E1388", {"start": v(-8.16, 3.61) * mm, "end": v(-8.65, 3.61) * mm});
            skLineSegment(sketch, "E1389", {"start": v(-8.65, 3.61) * mm, "end": v(-9, 3.58) * mm});
            skLineSegment(sketch, "E1390", {"start": v(-9, 3.58) * mm, "end": v(-9.25, 3.51) * mm});
            skLineSegment(sketch, "E1391", {"start": v(-9.25, 3.51) * mm, "end": v(-9.45, 3.4) * mm});
            skLineSegment(sketch, "E1392", {"start": v(-9.45, 3.4) * mm, "end": v(-9.65, 3.25) * mm});
            skLineSegment(sketch, "E1393", {"start": v(-9.65, 3.25) * mm, "end": v(-9.88, 3.04) * mm});
            skLineSegment(sketch, "E1394", {"start": v(-9.88, 3.04) * mm, "end": v(-10.2, 2.78) * mm});
            skLineSegment(sketch, "E1395", {"start": v(-10.2, 2.78) * mm, "end": v(-10.64, 2.45) * mm});
            skLineSegment(sketch, "E1396", {"start": v(-10.64, 2.45) * mm, "end": v(-11.13, 2.09) * mm});
            skLineSegment(sketch, "E1397", {"start": v(-11.13, 2.09) * mm, "end": v(-11.3, 1.94) * mm});
            skLineSegment(sketch, "E1398", {"start": v(-11.3, 1.94) * mm, "end": v(-11.4, 1.84) * mm});
            skLineSegment(sketch, "E1399", {"start": v(-11.4, 1.84) * mm, "end": v(-11.47, 1.74) * mm});
            skLineSegment(sketch, "E1400", {"start": v(-11.47, 1.74) * mm, "end": v(-11.53, 1.6) * mm});
            skSolve(sketch);
        }
        {
            var Q0;
            Q0=makeQuery(id+"F2.imprint","IMPRINT",FACE,{"disambiguationData":[TD([[makeQuery(id+"F2.imprint","IMPRINT",EDGE,{"derivedFrom":sQuery(id+"F2.wireOp",EDGE,"E533")}),1.0]])]});
            var Q1;
            Q1=makeQuery(id+"F2.imprint","IMPRINT",FACE,{"disambiguationData":[TD([[makeQuery(id+"F2.imprint","IMPRINT",EDGE,{"derivedFrom":sQuery(id+"F2.wireOp",EDGE,"E644")}),1.0]])]});
            var Q2;
            Q2=makeQuery(id+"F2.imprint","IMPRINT",FACE,{"disambiguationData":[TD([[makeQuery(id+"F2.imprint","IMPRINT",EDGE,{"derivedFrom":sQuery(id+"F2.wireOp",EDGE,"E995")}),1.0]])]});
            var Q3;
            Q3=makeQuery(id+"F2.imprint","IMPRINT",FACE,{"disambiguationData":[TD([[makeQuery(id+"F2.imprint","IMPRINT",EDGE,{"derivedFrom":sQuery(id+"F2.wireOp",EDGE,"E1068")}),1.0]])]});
            var Q4;
            Q4=makeQuery(id+"F2.imprint","IMPRINT",FACE,{"disambiguationData":[TD([[makeQuery(id+"F2.imprint","IMPRINT",EDGE,{"derivedFrom":sQuery(id+"F2.wireOp",EDGE,"E1")}),1.0]])]});
            extrude(context, id + "F3", {"entities" : qUnion([Q0, Q1, Q2, Q3, Q4]), "operationType" : NewBodyOperationType.ADD, "depth" : 3.17 * mm});
        }
        {
            var Q0;
            Q0=makeQuery(id+"F1.opExtrude","CAP_EDGE",EDGE,{"disambiguationData":[OSD([sQuery(id+"F0.wireOp",EDGE,"E0.bottom")])],"isStart":false});
            var Q1;
            Q1=makeQuery(id+"F1.opExtrude","CAP_EDGE",EDGE,{"disambiguationData":[OSD([sQuery(id+"F0.wireOp",EDGE,"E0.right")])],"isStart":false});
            var Q2;
            Q2=makeQuery(id+"F1.opExtrude","CAP_EDGE",EDGE,{"disambiguationData":[OSD([sQuery(id+"F0.wireOp",EDGE,"E0.top")])],"isStart":false});
            var Q3;
            Q3=makeQuery(id+"F1.opExtrude","CAP_EDGE",EDGE,{"disambiguationData":[OSD([sQuery(id+"F0.wireOp",EDGE,"E0.left")])],"isStart":false});
            fillet(context, id + "F4", {"entities" : qUnion([Q0, Q1, Q2, Q3]), "radius" : 5.08 * mm, "tangentPropagation" : true, "allowEdgeOverflow" : false});
        }
    });
